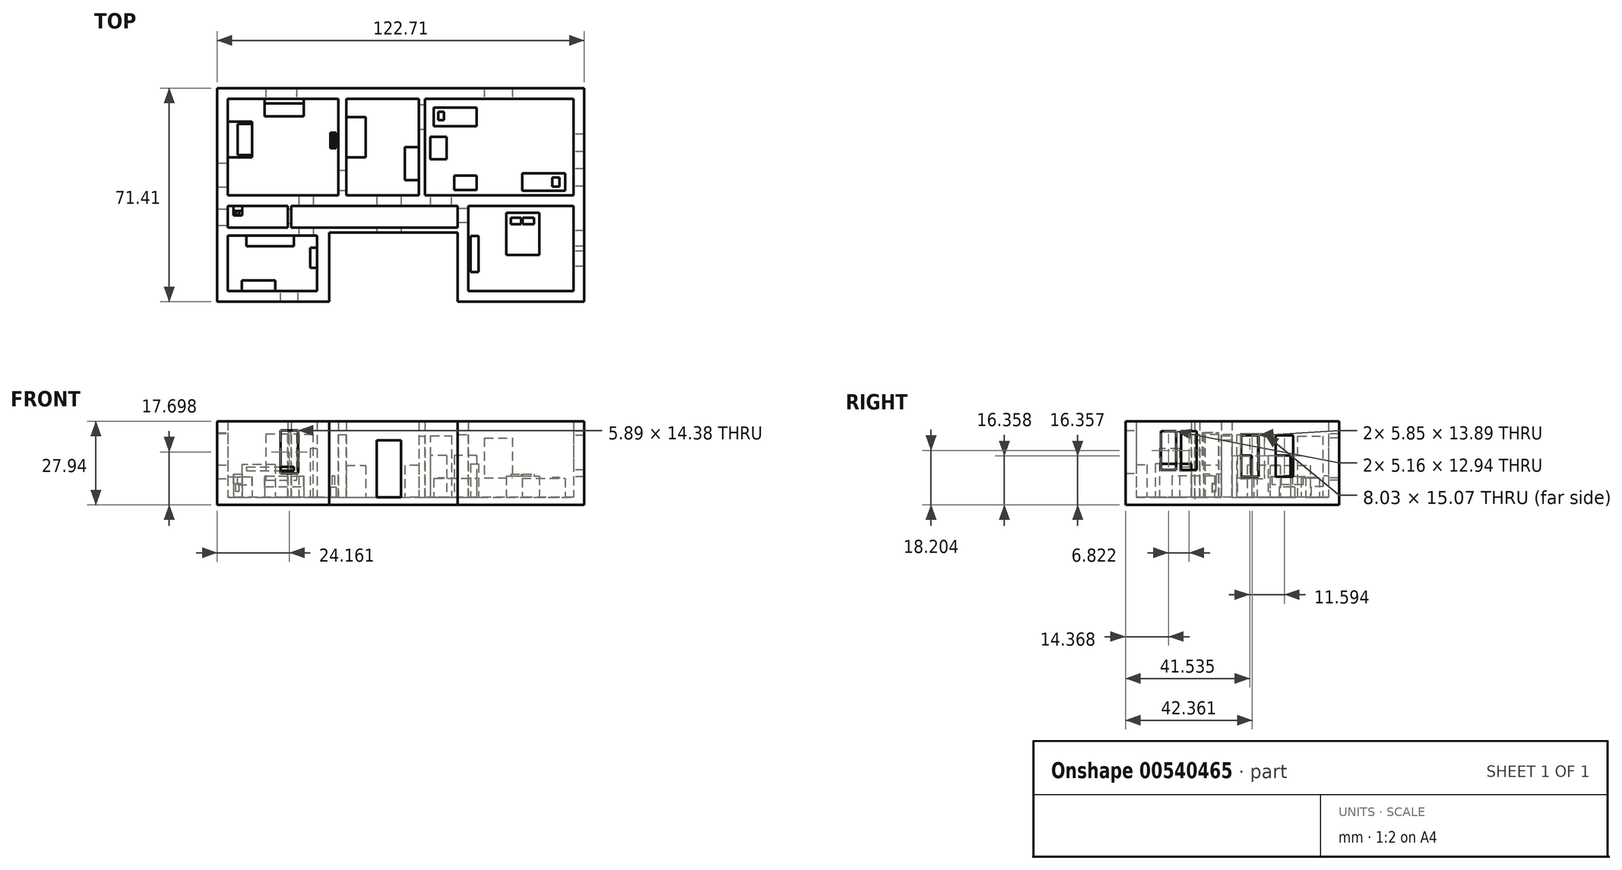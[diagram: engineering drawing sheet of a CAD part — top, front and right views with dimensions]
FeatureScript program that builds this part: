
annotation { "Feature Type Name" : "Feature", "Feature Type Description" : "" }
export const myFeature = defineFeature(function(context is Context, id is Id, definition is map)
    precondition{}
    {
        {
            var Q0;
            Q0=qCreatedBy(makeId("Top.planeOp"),FACE);
            var sketch = newSketch(context, id + "F0", { "sketchPlane" : qUnion([Q0])});
            skLineSegment(sketch, "E0", {"start": v(-23.01, 3.91) * mm, "end": v(21.3, 3.91) * mm});
            skLineSegment(sketch, "E1", {"start": v(62.73, 39.77) * mm, "end": v(62.73, 7.47) * mm});
            skLineSegment(sketch, "E2", {"start": v(62.73, 3.91) * mm, "end": v(27.52, 3.91) * mm});
            skLineSegment(sketch, "E3", {"start": v(62.73, 3.91) * mm, "end": v(62.73, -24.54) * mm});
            skLineSegment(sketch, "E4", {"start": v(62.73, -24.54) * mm, "end": v(27.52, -24.54) * mm});
            skLineSegment(sketch, "E5", {"start": v(27.52, -24.54) * mm, "end": v(27.52, -3.34) * mm});
            skLineSegment(sketch, "E6", {"start": v(27.52, -3.34) * mm, "end": v(-23.01, -3.34) * mm});
            skLineSegment(sketch, "E7", {"start": v(-23.01, -3.34) * mm, "end": v(-23.01, -24.54) * mm});
            skLineSegment(sketch, "E8", {"start": v(-23.01, -24.54) * mm, "end": v(-52.8, -24.54) * mm});
            skLineSegment(sketch, "E9", {"start": v(-52.8, -24.54) * mm, "end": v(-52.8, -6.04) * mm});
            skLineSegment(sketch, "E10", {"start": v(-52.8, -3.34) * mm, "end": v(-30.46, -3.34) * mm});
            skLineSegment(sketch, "E11", {"start": v(-52.8, -3.34) * mm, "end": v(-52.8, 3.91) * mm});
            skLineSegment(sketch, "E12", {"start": v(-52.8, 7.47) * mm, "end": v(-52.8, 39.77) * mm});
            skLineSegment(sketch, "E13", {"start": v(62.73, 39.77) * mm, "end": v(13.01, 39.77) * mm});
            skLineSegment(sketch, "E14", {"start": v(10.98, 39.77) * mm, "end": v(10.98, 35) * mm});
            skLineSegment(sketch, "E15", {"start": v(-52.8, 39.77) * mm, "end": v(-15.94, 39.77) * mm});
            skLineSegment(sketch, "E16", {"start": v(-15.94, 39.77) * mm, "end": v(-15.94, 11.85) * mm});
            skLineSegment(sketch, "E17.trimOffspring", {"start": v(10.98, 30.8) * mm, "end": v(10.98, 7.47) * mm});
            skLineSegment(sketch, "E18", {"start": v(-56.43, 43.32) * mm, "end": v(-56.43, -28.1) * mm});
            skLineSegment(sketch, "E19", {"start": v(-56.43, -28.1) * mm, "end": v(-19, -28.1) * mm});
            skLineSegment(sketch, "E20", {"start": v(-19, -28.1) * mm, "end": v(-19, -4.99) * mm});
            skLineSegment(sketch, "E21", {"start": v(-19, -4.99) * mm, "end": v(23.96, -4.99) * mm});
            skLineSegment(sketch, "E22", {"start": v(23.96, -4.99) * mm, "end": v(23.96, -28.1) * mm});
            skLineSegment(sketch, "E23", {"start": v(23.96, -28.1) * mm, "end": v(66.28, -28.1) * mm});
            skLineSegment(sketch, "E24", {"start": v(66.28, -28.1) * mm, "end": v(66.28, 43.32) * mm});
            skLineSegment(sketch, "E25", {"start": v(66.28, 43.32) * mm, "end": v(-56.43, 43.32) * mm});
            skLineSegment(sketch, "E26", {"start": v(-52.8, -6.04) * mm, "end": v(-30.46, -6.04) * mm});
            skLineSegment(sketch, "E27", {"start": v(-30.46, -6.04) * mm, "end": v(-30.46, -3.34) * mm});
            skLineSegment(sketch, "E28", {"start": v(-52.8, 3.91) * mm, "end": v(-30.46, 3.91) * mm});
            skLineSegment(sketch, "E29", {"start": v(-30.46, 3.91) * mm, "end": v(-30.46, 7.47) * mm});
            skLineSegment(sketch, "E30", {"start": v(-30.46, 7.47) * mm, "end": v(-52.8, 7.47) * mm});
            skLineSegment(sketch, "E31", {"start": v(-15.94, 7.47) * mm, "end": v(-23.01, 7.47) * mm});
            skLineSegment(sketch, "E32", {"start": v(-23.01, 7.47) * mm, "end": v(-23.01, 3.91) * mm});
            skLineSegment(sketch, "E33", {"start": v(-15.94, 7.47) * mm, "end": v(10.98, 7.47) * mm});
            skLineSegment(sketch, "E34", {"start": v(13.01, 7.47) * mm, "end": v(21.3, 7.47) * mm});
            skLineSegment(sketch, "E35", {"start": v(21.3, 7.47) * mm, "end": v(21.3, 3.91) * mm});
            skLineSegment(sketch, "E36", {"start": v(27.52, 7.47) * mm, "end": v(62.73, 7.47) * mm});
            skLineSegment(sketch, "E37", {"start": v(27.52, 3.91) * mm, "end": v(27.52, 7.47) * mm});
            skLineSegment(sketch, "E38", {"start": v(13.01, 7.47) * mm, "end": v(13.01, 30.8) * mm});
            skLineSegment(sketch, "E39", {"start": v(13.01, 30.8) * mm, "end": v(10.98, 30.8) * mm});
            skLineSegment(sketch, "E40", {"start": v(13.01, 35) * mm, "end": v(13.01, 39.77) * mm});
            skLineSegment(sketch, "E41", {"start": v(10.98, 35) * mm, "end": v(13.01, 35) * mm});
            skLineSegment(sketch, "E42", {"start": v(-13.3, 11.85) * mm, "end": v(-13.3, 39.77) * mm});
            skLineSegment(sketch, "E43", {"start": v(-15.94, 11.85) * mm, "end": v(-13.3, 11.85) * mm});
            skLineSegment(sketch, "E44", {"start": v(-13.3, 39.77) * mm, "end": v(10.98, 39.77) * mm});
            skLineSegment(sketch, "E45", {"start": v(21.3, 3.91) * mm, "end": v(27.52, 3.91) * mm});
            skLineSegment(sketch, "E46", {"start": v(27.52, 7.47) * mm, "end": v(21.3, 7.47) * mm});
            skLineSegment(sketch, "E47", {"start": v(27.52, -3.34) * mm, "end": v(27.52, 3.91) * mm});
            skLineSegment(sketch, "E48", {"start": v(-30.46, -3.34) * mm, "end": v(-23.01, -3.34) * mm});
            skLineSegment(sketch, "E49", {"start": v(-30.46, -6.04) * mm, "end": v(-23.01, -6.04) * mm});
            skLineSegment(sketch, "E50", {"start": v(-23.01, 3.91) * mm, "end": v(-30.46, 3.91) * mm});
            skLineSegment(sketch, "E51", {"start": v(-30.46, 7.47) * mm, "end": v(-23.01, 7.47) * mm});
            skLineSegment(sketch, "E52", {"start": v(10.98, 30.8) * mm, "end": v(10.98, 35) * mm});
            skLineSegment(sketch, "E53", {"start": v(13.01, 35) * mm, "end": v(13.01, 30.8) * mm});
            skLineSegment(sketch, "E54", {"start": v(-15.94, 7.47) * mm, "end": v(-15.94, 11.85) * mm});
            skLineSegment(sketch, "E55", {"start": v(-13.3, 11.85) * mm, "end": v(-13.3, 7.47) * mm});
            skLineSegment(sketch, "E56", {"start": v(27.95, 3.91) * mm, "end": v(27.95, -3.34) * mm});
            skLineSegment(sketch, "E57", {"start": v(-30.46, 3.91) * mm, "end": v(-30.46, -3.34) * mm});
            skLineSegment(sketch, "E58", {"start": v(-32.55, 3.91) * mm, "end": v(-32.55, -3.34) * mm});
            skSolve(sketch);
        }
        {
            var Q0;
            Q0 = qSketchRegion(id + "F0", true);
            var Q1;
            Q1=makeQuery(id+"F0.imprint","IMPRINT",FACE,{"disambiguationData":[TD([[makeQuery(id+"F0.imprint","IMPRINT",EDGE,{"derivedFrom":sQuery(id+"F0.wireOp",EDGE,"E29")}),-1.0]])]});
            var Q2;
            Q2=makeQuery(id+"F0.imprint","IMPRINT",FACE,{"disambiguationData":[TD([[makeQuery(id+"F0.imprint","IMPRINT",EDGE,{"derivedFrom":sQuery(id+"F0.wireOp",EDGE,"E43")}),-1.0]])]});
            var Q3;
            Q3=makeQuery(id+"F0.imprint","IMPRINT",FACE,{"disambiguationData":[TD([[makeQuery(id+"F0.imprint","IMPRINT",EDGE,{"derivedFrom":sQuery(id+"F0.wireOp",EDGE,"E0")}),1.0]])]});
            var Q4;
            Q4=makeQuery(id+"F0.imprint","IMPRINT",FACE,{"disambiguationData":[TD([[makeQuery(id+"F0.imprint","IMPRINT",EDGE,{"derivedFrom":sQuery(id+"F0.wireOp",EDGE,"E27")}),-1.0]])]});
            var Q5;
            Q5=makeQuery(id+"F0.imprint","IMPRINT",FACE,{"disambiguationData":[TD([[makeQuery(id+"F0.imprint","IMPRINT",EDGE,{"derivedFrom":sQuery(id+"F0.wireOp",EDGE,"E35")}),1.0]])]});
            var Q6;
            Q6=makeQuery(id+"F0.imprint","IMPRINT",FACE,{"disambiguationData":[TD([[makeQuery(id+"F0.imprint","IMPRINT",EDGE,{"derivedFrom":sQuery(id+"F0.wireOp",EDGE,"E39")}),-1.0]])]});
            var Q7;
            {var subQ0=sQuery(id+"F0.wireOp",EDGE,"E47");Q7=makeQuery(id+"F0.imprint","IMPRINT",FACE,{"disambiguationData":[TD([[makeQuery(id+"F0.imprint","IMPRINT",EDGE,{"derivedFrom":subQ0}),1.0]])]});}
            var Q8;
            {var subQ0=sQuery(id+"F0.wireOp",EDGE,"E57");Q8=makeQuery(id+"F0.imprint","IMPRINT",FACE,{"disambiguationData":[TD([[makeQuery(id+"F0.imprint","IMPRINT",EDGE,{"derivedFrom":subQ0}),-1.0]])]});}
            extrude(context, id + "F1", {"entities" : qUnion([Q0, Q1, Q2, Q3, Q4, Q5, Q6, Q7, Q8]), "depth" : 25.4 * mm, "offsetDistance" : 25.4 * mm});
        }
        {
            var Q0;
            Q0=makeQuery(id+"F1.opExtrude","CAP_FACE",FACE,{"disambiguationData":[OSD([sQuery(id+"F0.wireOp",EDGE,"E0"),sQuery(id+"F0.wireOp",EDGE,"E1"),sQuery(id+"F0.wireOp",EDGE,"E2"),sQuery(id+"F0.wireOp",EDGE,"E3"),sQuery(id+"F0.wireOp",EDGE,"E4"),sQuery(id+"F0.wireOp",EDGE,"E5"),sQuery(id+"F0.wireOp",EDGE,"E6"),sQuery(id+"F0.wireOp",EDGE,"E7"),sQuery(id+"F0.wireOp",EDGE,"E8"),sQuery(id+"F0.wireOp",EDGE,"E9"),sQuery(id+"F0.wireOp",EDGE,"E10"),sQuery(id+"F0.wireOp",EDGE,"E11"),sQuery(id+"F0.wireOp",EDGE,"E12"),sQuery(id+"F0.wireOp",EDGE,"E13"),sQuery(id+"F0.wireOp",EDGE,"E14"),sQuery(id+"F0.wireOp",EDGE,"E15"),sQuery(id+"F0.wireOp",EDGE,"E16"),sQuery(id+"F0.wireOp",EDGE,"E17.trimOffspring"),sQuery(id+"F0.wireOp",EDGE,"E18"),sQuery(id+"F0.wireOp",EDGE,"E19"),sQuery(id+"F0.wireOp",EDGE,"E20"),sQuery(id+"F0.wireOp",EDGE,"E21"),sQuery(id+"F0.wireOp",EDGE,"E22"),sQuery(id+"F0.wireOp",EDGE,"E23"),sQuery(id+"F0.wireOp",EDGE,"E24"),sQuery(id+"F0.wireOp",EDGE,"E25"),sQuery(id+"F0.wireOp",EDGE,"E26"),sQuery(id+"F0.wireOp",EDGE,"E28"),sQuery(id+"F0.wireOp",EDGE,"E30"),sQuery(id+"F0.wireOp",EDGE,"E31"),sQuery(id+"F0.wireOp",EDGE,"E33"),sQuery(id+"F0.wireOp",EDGE,"E34"),sQuery(id+"F0.wireOp",EDGE,"E36"),sQuery(id+"F0.wireOp",EDGE,"E38"),sQuery(id+"F0.wireOp",EDGE,"E40"),sQuery(id+"F0.wireOp",EDGE,"E42"),sQuery(id+"F0.wireOp",EDGE,"E44"),sQuery(id+"F0.wireOp",EDGE,"E45"),sQuery(id+"F0.wireOp",EDGE,"E46"),sQuery(id+"F0.wireOp",EDGE,"E47"),sQuery(id+"F0.wireOp",EDGE,"E48"),sQuery(id+"F0.wireOp",EDGE,"E49"),sQuery(id+"F0.wireOp",EDGE,"E50"),sQuery(id+"F0.wireOp",EDGE,"E51"),sQuery(id+"F0.wireOp",EDGE,"E52"),sQuery(id+"F0.wireOp",EDGE,"E53"),sQuery(id+"F0.wireOp",EDGE,"E54"),sQuery(id+"F0.wireOp",EDGE,"E55"),sQuery(id+"F0.wireOp",EDGE,"E56"),sQuery(id+"F0.wireOp",EDGE,"E57"),sQuery(id+"F0.wireOp",EDGE,"E58")])],"isStart":true});
            var sketch = newSketch(context, id + "F2", { "sketchPlane" : qUnion([Q0])});
            skLineSegment(sketch, "E59.bottom", {"start": v(-56.43, 28.1) * mm, "end": v(66.28, 28.1) * mm});
            skLineSegment(sketch, "E59.top", {"start": v(-56.43, -43.32) * mm, "end": v(66.28, -43.32) * mm});
            skLineSegment(sketch, "E59.left", {"start": v(-56.43, 28.1) * mm, "end": v(-56.43, -43.32) * mm});
            skLineSegment(sketch, "E59.right", {"start": v(66.28, 28.1) * mm, "end": v(66.28, -43.32) * mm});
            skSolve(sketch);
        }
        {
            var Q0;
            Q0 = qSketchRegion(id + "F2", true);
            extrude(context, id + "F3", {"entities" : qUnion([Q0]), "operationType" : NewBodyOperationType.ADD, "depth" : 2.54 * mm, "offsetDistance" : 25.4 * mm});
        }
        {
            var Q0;
            Q0=makeQuery(id+"F1.opExtrude","SWEPT_FACE",FACE,{"disambiguationData":[OSD([sQuery(id+"F0.wireOp",EDGE,"E21")])]});
            var sketch = newSketch(context, id + "F4", { "sketchPlane" : qUnion([Q0])});
            skLineSegment(sketch, "E60", {"start": v(-3.06, 0) * mm, "end": v(-3.06, 19.08) * mm});
            skLineSegment(sketch, "E61", {"start": v(-3.06, 19.08) * mm, "end": v(5.05, 19.08) * mm});
            skLineSegment(sketch, "E62", {"start": v(5.05, 19.08) * mm, "end": v(5.05, 0) * mm});
            skSolve(sketch);
        }
        {
            var Q0;
            Q0=makeQuery(id+"F1.opExtrude","SWEPT_FACE",FACE,{"disambiguationData":[OSD([sQuery(id+"F0.wireOp",EDGE,"E5"),sQuery(id+"F0.wireOp",EDGE,"E47")])]});
            var sketch = newSketch(context, id + "F5", { "sketchPlane" : qUnion([Q0])});
            skLineSegment(sketch, "E63", {"start": v(-1.5, 0) * mm, "end": v(-1.5, 21) * mm});
            skLineSegment(sketch, "E64", {"start": v(-1.5, 21) * mm, "end": v(3.2, 21) * mm});
            skLineSegment(sketch, "E65", {"start": v(3.2, 21) * mm, "end": v(3.2, 0) * mm});
            skSolve(sketch);
        }
        {
            var Q0;
            Q0=makeQuery(id+"F1.opExtrude","SWEPT_FACE",FACE,{"disambiguationData":[OSD([sQuery(id+"F0.wireOp",EDGE,"E26"),sQuery(id+"F0.wireOp",EDGE,"E49")])]});
            var sketch = newSketch(context, id + "F6", { "sketchPlane" : qUnion([Q0])});
            skLineSegment(sketch, "E66", {"start": v(-29.15, 0) * mm, "end": v(-29.15, 20.99) * mm});
            skLineSegment(sketch, "E67", {"start": v(-29.15, 20.99) * mm, "end": v(-24.32, 20.99) * mm});
            skLineSegment(sketch, "E68", {"start": v(-24.32, 20.99) * mm, "end": v(-24.32, 0) * mm});
            skSolve(sketch);
        }
        {
            var Q0;
            Q0=makeQuery(id+"F1.opExtrude","SWEPT_FACE",FACE,{"disambiguationData":[OSD([sQuery(id+"F0.wireOp",EDGE,"E42"),sQuery(id+"F0.wireOp",EDGE,"E55")])]});
            var sketch = newSketch(context, id + "F7", { "sketchPlane" : qUnion([Q0])});
            skLineSegment(sketch, "E69", {"start": v(9.12, 0) * mm, "end": v(9.12, 20.96) * mm});
            skLineSegment(sketch, "E70", {"start": v(9.12, 20.96) * mm, "end": v(15.83, 20.96) * mm});
            skLineSegment(sketch, "E71", {"start": v(15.83, 20.96) * mm, "end": v(15.83, 0) * mm});
            skSolve(sketch);
        }
        {
            var Q0;
            Q0=makeQuery(id+"F1.opExtrude","SWEPT_FACE",FACE,{"disambiguationData":[OSD([sQuery(id+"F0.wireOp",EDGE,"E38"),sQuery(id+"F0.wireOp",EDGE,"E40"),sQuery(id+"F0.wireOp",EDGE,"E53")])]});
            var sketch = newSketch(context, id + "F8", { "sketchPlane" : qUnion([Q0])});
            skLineSegment(sketch, "E72", {"start": v(29.52, 0) * mm, "end": v(29.52, 20.52) * mm});
            skLineSegment(sketch, "E73", {"start": v(29.52, 20.52) * mm, "end": v(37.83, 20.52) * mm});
            skLineSegment(sketch, "E74", {"start": v(37.83, 20.52) * mm, "end": v(37.83, 0) * mm});
            skSolve(sketch);
        }
        {
            var Q0;
            Q0=makeQuery(id+"F1.opExtrude","SWEPT_FACE",FACE,{"disambiguationData":[OSD([sQuery(id+"F0.wireOp",EDGE,"E34"),sQuery(id+"F0.wireOp",EDGE,"E36"),sQuery(id+"F0.wireOp",EDGE,"E46")])]});
            var sketch = newSketch(context, id + "F9", { "sketchPlane" : qUnion([Q0])});
            skLineSegment(sketch, "E75", {"start": v(-14.91, 0) * mm, "end": v(-14.91, 20.6) * mm});
            skLineSegment(sketch, "E76", {"start": v(-14.91, 20.6) * mm, "end": v(-21.93, 20.6) * mm});
            skLineSegment(sketch, "E77", {"start": v(-21.93, 20.6) * mm, "end": v(-21.93, 0) * mm});
            skSolve(sketch);
        }
        {
            var Q0;
            {var subQ0=sQuery(id+"F0.wireOp",EDGE,"E46");var subQ1=sQuery(id+"F0.wireOp",EDGE,"E36");var subQ2=sQuery(id+"F0.wireOp",EDGE,"E34");var subQ3=sQuery(id+"F0.wireOp",EDGE,"E53");var subQ4=sQuery(id+"F0.wireOp",EDGE,"E40");var subQ5=sQuery(id+"F0.wireOp",EDGE,"E38");var subQ6=sQuery(id+"F0.wireOp",EDGE,"E55");var subQ7=sQuery(id+"F0.wireOp",EDGE,"E42");var subQ8=sQuery(id+"F0.wireOp",EDGE,"E57");var subQ9=sQuery(id+"F0.wireOp",EDGE,"E49");var subQ10=sQuery(id+"F0.wireOp",EDGE,"E26");var subQ11=sQuery(id+"F0.wireOp",EDGE,"E47");var subQ12=sQuery(id+"F0.wireOp",EDGE,"E5");var subQ13=sQuery(id+"F0.wireOp",EDGE,"E21");var subQ14=sQuery(id+"F2.wireOp",EDGE,"E59.bottom");var subQ15=makeQuery(id+"F3.opExtrude","CAP_FACE",FACE,{"disambiguationData":[OSD([subQ14,sQuery(id+"F2.wireOp",EDGE,"E59.top"),sQuery(id+"F2.wireOp",EDGE,"E59.left"),sQuery(id+"F2.wireOp",EDGE,"E59.right")])],"isStart":true});Q0=makeQuery(id+"F1OyW4JsobVm1jb_1.boolean.opBoolean","MERGE",FACE,{"derivedFrom":[makeQuery(id+"FLEFhuE11UkbnLt_1.boolean.opBoolean","MERGE",FACE,{"derivedFrom":[makeQuery(id+"F3.boolean.opBoolean","SPLIT",FACE,{"disambiguationData":[TD([makeQuery(id+"F1.opExtrude","SWEPT_FACE",FACE,{"disambiguationData":[OSD([sQuery(id+"F0.wireOp",EDGE,"E1")])]})])],"derivedFrom":subQ15}),makeQuery(id+"FrTdRAxnjzJTjCx_1.boolean.opBoolean","MERGE",FACE,{"derivedFrom":[makeQuery(id+"F3DeUZIcQ9rfyYD_1.boolean.opBoolean","MERGE",FACE,{"derivedFrom":[makeQuery(id+"F3.boolean.opBoolean","SPLIT",FACE,{"disambiguationData":[TD([makeQuery(id+"F1.opExtrude","SWEPT_FACE",FACE,{"disambiguationData":[OSD([sQuery(id+"F0.wireOp",EDGE,"E10")])]})])],"derivedFrom":subQ15}),makeQuery(id+"FgtxtSheF1BaROL_1.boolean.opBoolean","MERGE",FACE,{"derivedFrom":[makeQuery(id+"F3.boolean.opBoolean","SPLIT",FACE,{"disambiguationData":[TD([makeQuery(id+"F1.opExtrude","SWEPT_FACE",FACE,{"disambiguationData":[OSD([sQuery(id+"F0.wireOp",EDGE,"E7")])]})])],"derivedFrom":subQ15}),makeQuery(id+"F3.boolean.opBoolean","SPLIT",FACE,{"disambiguationData":[TD([makeQuery(id+"F1.opExtrude","SWEPT_FACE",FACE,{"disambiguationData":[OSD([sQuery(id+"F0.wireOp",EDGE,"E12")])]})])],"derivedFrom":subQ15}),makeQuery(id+"F2jdueuljUY2eIT_1.boolean.opBoolean","MERGE",FACE,{"derivedFrom":[makeQuery(id+"F3.boolean.opBoolean","SPLIT",FACE,{"disambiguationData":[TD([makeQuery(id+"F1.opExtrude","SWEPT_FACE",FACE,{"disambiguationData":[OSD([sQuery(id+"F0.wireOp",EDGE,"E2")])]})])],"derivedFrom":subQ15}),makeQuery(id+"Fv9FIk8MfVWjiKt_1.boolean.opBoolean","MERGE",FACE,{"derivedFrom":[makeQuery(id+"F3.boolean.opBoolean","SPLIT",FACE,{"disambiguationData":[TD([makeQuery(id+"F1.opExtrude","SWEPT_FACE",FACE,{"disambiguationData":[OSD([sQuery(id+"F0.wireOp",EDGE,"E56")])]})])],"derivedFrom":subQ15}),makeQuery(id+"F3.boolean.opBoolean","SPLIT",FACE,{"disambiguationData":[TD([makeQuery(id+"F1.opExtrude","SWEPT_FACE",FACE,{"disambiguationData":[OSD([sQuery(id+"F0.wireOp",EDGE,"E33")])]})])],"derivedFrom":subQ15}),makeQuery(id+"F3.boolean.opBoolean","SPLIT",FACE,{"disambiguationData":[TD([makeQuery(id+"F1.opExtrude","SWEPT_FACE",FACE,{"disambiguationData":[OSD([sQuery(id+"F0.wireOp",EDGE,"E19")])]})])],"derivedFrom":subQ15}),makeQuery(id+"Fv9FIk8MfVWjiKt_1.opExtrude","SWEPT_FACE",FACE,{"disambiguationData":[OSD([subQ13])]})]}),makeQuery(id+"F2jdueuljUY2eIT_1.opExtrude","SWEPT_FACE",FACE,{"disambiguationData":[OSD([subQ12,subQ11])]})]}),makeQuery(id+"FgtxtSheF1BaROL_1.opExtrude","SWEPT_FACE",FACE,{"disambiguationData":[OSD([subQ10,subQ9])]})]}),makeQuery(id+"F3DeUZIcQ9rfyYD_1.opExtrude","SWEPT_FACE",FACE,{"disambiguationData":[OSD([subQ8])]})]}),makeQuery(id+"FrTdRAxnjzJTjCx_1.opExtrude","SWEPT_FACE",FACE,{"disambiguationData":[OSD([subQ7,subQ6])]})]}),makeQuery(id+"FLEFhuE11UkbnLt_1.opExtrude","SWEPT_FACE",FACE,{"disambiguationData":[OSD([subQ5,subQ4,subQ3])]})]}),makeQuery(id+"F1OyW4JsobVm1jb_1.opExtrude","SWEPT_FACE",FACE,{"disambiguationData":[OSD([subQ2,subQ1,subQ0])]})]});}
            var sketch = newSketch(context, id + "F10", { "sketchPlane" : qUnion([Q0])});
            skLineSegment(sketch, "E78.bottom", {"start": v(-19, -4.99) * mm, "end": v(23.96, -4.99) * mm});
            skLineSegment(sketch, "E78.top", {"start": v(-19, -28.1) * mm, "end": v(23.96, -28.1) * mm});
            skLineSegment(sketch, "E78.left", {"start": v(-19, -4.99) * mm, "end": v(-19, -28.1) * mm});
            skLineSegment(sketch, "E78.right", {"start": v(23.96, -4.99) * mm, "end": v(23.96, -28.1) * mm});
            skSolve(sketch);
        }
        {
            var Q0;
            Q0 = qSketchRegion(id + "F10", true);
            extrude(context, id + "F11", {"entities" : qUnion([Q0]), "operationType" : NewBodyOperationType.REMOVE, "oppositeDirection" : true, "depth" : 25.4 * mm, "offsetDistance" : 25.4 * mm});
        }
        {
            var Q0;
            Q0=makeQuery(id+"F1.opExtrude","CAP_FACE",FACE,{"disambiguationData":[OSD([sQuery(id+"F0.wireOp",EDGE,"E1"),sQuery(id+"F0.wireOp",EDGE,"E2"),sQuery(id+"F0.wireOp",EDGE,"E3"),sQuery(id+"F0.wireOp",EDGE,"E4"),sQuery(id+"F0.wireOp",EDGE,"E5"),sQuery(id+"F0.wireOp",EDGE,"E7"),sQuery(id+"F0.wireOp",EDGE,"E8"),sQuery(id+"F0.wireOp",EDGE,"E9"),sQuery(id+"F0.wireOp",EDGE,"E10"),sQuery(id+"F0.wireOp",EDGE,"E11"),sQuery(id+"F0.wireOp",EDGE,"E12"),sQuery(id+"F0.wireOp",EDGE,"E13"),sQuery(id+"F0.wireOp",EDGE,"E14"),sQuery(id+"F0.wireOp",EDGE,"E15"),sQuery(id+"F0.wireOp",EDGE,"E16"),sQuery(id+"F0.wireOp",EDGE,"E17.trimOffspring"),sQuery(id+"F0.wireOp",EDGE,"E18"),sQuery(id+"F0.wireOp",EDGE,"E19"),sQuery(id+"F0.wireOp",EDGE,"E20"),sQuery(id+"F0.wireOp",EDGE,"E21"),sQuery(id+"F0.wireOp",EDGE,"E22"),sQuery(id+"F0.wireOp",EDGE,"E23"),sQuery(id+"F0.wireOp",EDGE,"E24"),sQuery(id+"F0.wireOp",EDGE,"E25"),sQuery(id+"F0.wireOp",EDGE,"E26"),sQuery(id+"F0.wireOp",EDGE,"E28"),sQuery(id+"F0.wireOp",EDGE,"E30"),sQuery(id+"F0.wireOp",EDGE,"E31"),sQuery(id+"F0.wireOp",EDGE,"E33"),sQuery(id+"F0.wireOp",EDGE,"E34"),sQuery(id+"F0.wireOp",EDGE,"E36"),sQuery(id+"F0.wireOp",EDGE,"E38"),sQuery(id+"F0.wireOp",EDGE,"E40"),sQuery(id+"F0.wireOp",EDGE,"E42"),sQuery(id+"F0.wireOp",EDGE,"E44"),sQuery(id+"F0.wireOp",EDGE,"E46"),sQuery(id+"F0.wireOp",EDGE,"E47"),sQuery(id+"F0.wireOp",EDGE,"E49"),sQuery(id+"F0.wireOp",EDGE,"E51"),sQuery(id+"F0.wireOp",EDGE,"E52"),sQuery(id+"F0.wireOp",EDGE,"E53"),sQuery(id+"F0.wireOp",EDGE,"E54"),sQuery(id+"F0.wireOp",EDGE,"E55"),sQuery(id+"F0.wireOp",EDGE,"E58")])],"isStart":false});
            var sketch = newSketch(context, id + "F12", { "sketchPlane" : qUnion([Q0])});
            skLineSegment(sketch, "E79.bottom", {"start": v(-28.74, 3.91) * mm, "end": v(23.96, 3.91) * mm});
            skLineSegment(sketch, "E79.top", {"start": v(-28.74, -3.34) * mm, "end": v(23.96, -3.34) * mm});
            skLineSegment(sketch, "E79.left", {"start": v(-28.74, 3.91) * mm, "end": v(-28.74, -3.34) * mm});
            skLineSegment(sketch, "E79.right", {"start": v(23.96, 3.91) * mm, "end": v(23.96, -3.34) * mm});
            skSolve(sketch);
        }
        {
            var Q0;
            Q0=makeQuery(id+"F12.imprint","IMPRINT",FACE,{"disambiguationData":[TD([[makeQuery(id+"F12.imprint","IMPRINT",EDGE,{"derivedFrom":sQuery(id+"F12.wireOp",EDGE,"E79.bottom")}),-1.0]])]});
            var Q1;
            Q1=makeQuery(id+"F3.opExtrude","CAP_FACE",FACE,{"disambiguationData":[OSD([sQuery(id+"F2.wireOp",EDGE,"E59.bottom"),sQuery(id+"F2.wireOp",EDGE,"E59.top"),sQuery(id+"F2.wireOp",EDGE,"E59.left"),sQuery(id+"F2.wireOp",EDGE,"E59.right")])],"isStart":false});
            extrude(context, id + "F13", {"entities" : qUnion([Q0]), "operationType" : NewBodyOperationType.REMOVE, "oppositeDirection" : true, "depth" : 25.4 * mm, "endBoundEntityFace" : qUnion([Q1]), "offsetDistance" : 25.4 * mm});
        }
        {
            var Q0;
            Q0=makeQuery(id+"F1.opExtrude","CAP_FACE",FACE,{"disambiguationData":[OSD([sQuery(id+"F0.wireOp",EDGE,"E1"),sQuery(id+"F0.wireOp",EDGE,"E2"),sQuery(id+"F0.wireOp",EDGE,"E3"),sQuery(id+"F0.wireOp",EDGE,"E4"),sQuery(id+"F0.wireOp",EDGE,"E5"),sQuery(id+"F0.wireOp",EDGE,"E7"),sQuery(id+"F0.wireOp",EDGE,"E8"),sQuery(id+"F0.wireOp",EDGE,"E9"),sQuery(id+"F0.wireOp",EDGE,"E10"),sQuery(id+"F0.wireOp",EDGE,"E11"),sQuery(id+"F0.wireOp",EDGE,"E12"),sQuery(id+"F0.wireOp",EDGE,"E13"),sQuery(id+"F0.wireOp",EDGE,"E14"),sQuery(id+"F0.wireOp",EDGE,"E15"),sQuery(id+"F0.wireOp",EDGE,"E16"),sQuery(id+"F0.wireOp",EDGE,"E17.trimOffspring"),sQuery(id+"F0.wireOp",EDGE,"E18"),sQuery(id+"F0.wireOp",EDGE,"E19"),sQuery(id+"F0.wireOp",EDGE,"E20"),sQuery(id+"F0.wireOp",EDGE,"E21"),sQuery(id+"F0.wireOp",EDGE,"E22"),sQuery(id+"F0.wireOp",EDGE,"E23"),sQuery(id+"F0.wireOp",EDGE,"E24"),sQuery(id+"F0.wireOp",EDGE,"E25"),sQuery(id+"F0.wireOp",EDGE,"E26"),sQuery(id+"F0.wireOp",EDGE,"E28"),sQuery(id+"F0.wireOp",EDGE,"E30"),sQuery(id+"F0.wireOp",EDGE,"E31"),sQuery(id+"F0.wireOp",EDGE,"E33"),sQuery(id+"F0.wireOp",EDGE,"E34"),sQuery(id+"F0.wireOp",EDGE,"E36"),sQuery(id+"F0.wireOp",EDGE,"E38"),sQuery(id+"F0.wireOp",EDGE,"E40"),sQuery(id+"F0.wireOp",EDGE,"E42"),sQuery(id+"F0.wireOp",EDGE,"E44"),sQuery(id+"F0.wireOp",EDGE,"E46"),sQuery(id+"F0.wireOp",EDGE,"E47"),sQuery(id+"F0.wireOp",EDGE,"E49"),sQuery(id+"F0.wireOp",EDGE,"E51"),sQuery(id+"F0.wireOp",EDGE,"E52"),sQuery(id+"F0.wireOp",EDGE,"E53"),sQuery(id+"F0.wireOp",EDGE,"E54"),sQuery(id+"F0.wireOp",EDGE,"E55"),sQuery(id+"F0.wireOp",EDGE,"E58")])],"isStart":false});
            var sketch = newSketch(context, id + "F14", { "sketchPlane" : qUnion([Q0])});
            skLineSegment(sketch, "E80.bottom", {"start": v(-32.55, -3.34) * mm, "end": v(-28.74, -3.34) * mm});
            skLineSegment(sketch, "E80.top", {"start": v(-32.55, 3.91) * mm, "end": v(-28.74, 3.91) * mm});
            skLineSegment(sketch, "E80.left", {"start": v(-32.55, -3.34) * mm, "end": v(-32.55, 3.91) * mm});
            skLineSegment(sketch, "E80.right", {"start": v(-28.74, -3.34) * mm, "end": v(-28.74, 3.91) * mm});
            skSolve(sketch);
        }
        {
            var Q0;
            Q0=makeQuery(id+"F14.imprint","IMPRINT",FACE,{"disambiguationData":[TD([[makeQuery(id+"F14.imprint","IMPRINT",EDGE,{"derivedFrom":sQuery(id+"F14.wireOp",EDGE,"E80.bottom")}),1.0]])]});
            extrude(context, id + "F15", {"entities" : qUnion([Q0]), "operationType" : NewBodyOperationType.REMOVE, "oppositeDirection" : true, "depth" : 25.4 * mm, "offsetDistance" : 25.4 * mm});
        }
        {
            var Q0;
            {var subQ0=sQuery(id+"F0.wireOp",EDGE,"E49");var subQ1=sQuery(id+"F0.wireOp",EDGE,"E26");var subQ2=sQuery(id+"F0.wireOp",EDGE,"E46");var subQ3=sQuery(id+"F0.wireOp",EDGE,"E36");var subQ4=sQuery(id+"F0.wireOp",EDGE,"E34");var subQ5=sQuery(id+"F0.wireOp",EDGE,"E53");var subQ6=sQuery(id+"F0.wireOp",EDGE,"E40");var subQ7=sQuery(id+"F0.wireOp",EDGE,"E38");var subQ8=sQuery(id+"F0.wireOp",EDGE,"E55");var subQ9=sQuery(id+"F0.wireOp",EDGE,"E42");var subQ10=sQuery(id+"F2.wireOp",EDGE,"E59.bottom");var subQ11=makeQuery(id+"F3.opExtrude","CAP_FACE",FACE,{"disambiguationData":[OSD([subQ10,sQuery(id+"F2.wireOp",EDGE,"E59.top"),sQuery(id+"F2.wireOp",EDGE,"E59.left"),sQuery(id+"F2.wireOp",EDGE,"E59.right")])],"isStart":true});var subQ12=sQuery(id+"F0.wireOp",EDGE,"E47");var subQ13=sQuery(id+"F0.wireOp",EDGE,"E5");var subQ14=sQuery(id+"F0.wireOp",EDGE,"E21");Q0=makeQuery(id+"F15.boolean.opBoolean","MERGE",FACE,{"derivedFrom":[makeQuery(id+"Fj91QTaVXWuzYNv_1.boolean.opBoolean","MERGE",FACE,{"derivedFrom":[makeQuery(id+"F3.boolean.opBoolean","SPLIT",FACE,{"disambiguationData":[TD([makeQuery(id+"F1.opExtrude","SWEPT_FACE",FACE,{"disambiguationData":[OSD([sQuery(id+"F0.wireOp",EDGE,"E10")])]})])],"derivedFrom":subQ11}),makeQuery(id+"F13.boolean.opBoolean","MERGE",FACE,{"derivedFrom":[makeQuery(id+"F1OyW4JsobVm1jb_1.boolean.opBoolean","MERGE",FACE,{"derivedFrom":[makeQuery(id+"FLEFhuE11UkbnLt_1.boolean.opBoolean","MERGE",FACE,{"derivedFrom":[makeQuery(id+"F3.boolean.opBoolean","SPLIT",FACE,{"disambiguationData":[TD([makeQuery(id+"F1.opExtrude","SWEPT_FACE",FACE,{"disambiguationData":[OSD([sQuery(id+"F0.wireOp",EDGE,"E1")])]})])],"derivedFrom":subQ11}),makeQuery(id+"FrTdRAxnjzJTjCx_1.boolean.opBoolean","MERGE",FACE,{"derivedFrom":[makeQuery(id+"F2jdueuljUY2eIT_1.boolean.opBoolean","MERGE",FACE,{"derivedFrom":[makeQuery(id+"F3.boolean.opBoolean","SPLIT",FACE,{"disambiguationData":[TD([makeQuery(id+"F1.opExtrude","SWEPT_FACE",FACE,{"disambiguationData":[OSD([sQuery(id+"F0.wireOp",EDGE,"E2")])]})])],"derivedFrom":subQ11}),makeQuery(id+"Fv9FIk8MfVWjiKt_1.boolean.opBoolean","MERGE",FACE,{"derivedFrom":[makeQuery(id+"F3.boolean.opBoolean","SPLIT",FACE,{"disambiguationData":[TD([makeQuery(id+"F1.opExtrude","SWEPT_FACE",FACE,{"disambiguationData":[OSD([sQuery(id+"F0.wireOp",EDGE,"E33")])]})])],"derivedFrom":subQ11}),makeQuery(id+"F3.boolean.opBoolean","SPLIT",FACE,{"disambiguationData":[TD([makeQuery(id+"F1.opExtrude","SWEPT_FACE",FACE,{"disambiguationData":[OSD([sQuery(id+"F0.wireOp",EDGE,"E19")])]})])],"derivedFrom":subQ11}),makeQuery(id+"Fv9FIk8MfVWjiKt_1.opExtrude","SWEPT_FACE",FACE,{"disambiguationData":[OSD([subQ14])]})]}),makeQuery(id+"F2jdueuljUY2eIT_1.opExtrude","SWEPT_FACE",FACE,{"disambiguationData":[OSD([subQ13,subQ12])]})]}),makeQuery(id+"FgtxtSheF1BaROL_1.boolean.opBoolean","MERGE",FACE,{"derivedFrom":[makeQuery(id+"F3.boolean.opBoolean","SPLIT",FACE,{"disambiguationData":[TD([makeQuery(id+"F1.opExtrude","SWEPT_FACE",FACE,{"disambiguationData":[OSD([sQuery(id+"F0.wireOp",EDGE,"E7")])]})])],"derivedFrom":subQ11}),makeQuery(id+"F3.boolean.opBoolean","SPLIT",FACE,{"disambiguationData":[TD([makeQuery(id+"F1.opExtrude","SWEPT_FACE",FACE,{"disambiguationData":[OSD([sQuery(id+"F0.wireOp",EDGE,"E12")])]})])],"derivedFrom":subQ11}),makeQuery(id+"FgtxtSheF1BaROL_1.opExtrude","SWEPT_FACE",FACE,{"disambiguationData":[OSD([subQ1,subQ0])]})]}),makeQuery(id+"FrTdRAxnjzJTjCx_1.opExtrude","SWEPT_FACE",FACE,{"disambiguationData":[OSD([subQ9,subQ8])]})]}),makeQuery(id+"FLEFhuE11UkbnLt_1.opExtrude","SWEPT_FACE",FACE,{"disambiguationData":[OSD([subQ7,subQ6,subQ5])]})]}),makeQuery(id+"F1OyW4JsobVm1jb_1.opExtrude","SWEPT_FACE",FACE,{"disambiguationData":[OSD([subQ4,subQ3,subQ2])]})]}),makeQuery(id+"F13.opExtrude","CAP_FACE",FACE,{"disambiguationData":[OSD([sQuery(id+"F12.wireOp",EDGE,"E79.bottom"),sQuery(id+"F12.wireOp",EDGE,"E79.top"),sQuery(id+"F12.wireOp",EDGE,"E79.left"),sQuery(id+"F12.wireOp",EDGE,"E79.right")])],"isStart":false})]}),makeQuery(id+"Fj91QTaVXWuzYNv_1.opExtrude","SWEPT_FACE",FACE,{"disambiguationData":[OSD([subQ1,subQ0,sQuery(id+"F6.wireOp",EDGE,"RrXdWSjr-arhV-RAkg-Kmuo-RMM0U9ZidCex")])]})]}),makeQuery(id+"F15.opExtrude","CAP_FACE",FACE,{"disambiguationData":[OSD([sQuery(id+"F14.wireOp",EDGE,"E80.bottom"),sQuery(id+"F14.wireOp",EDGE,"E80.top"),sQuery(id+"F14.wireOp",EDGE,"E80.left"),sQuery(id+"F14.wireOp",EDGE,"E80.right")])],"isStart":false})]});}
            var sketch = newSketch(context, id + "F16", { "sketchPlane" : qUnion([Q0])});
            skLineSegment(sketch, "E81", {"start": v(-32.8, 3.91) * mm, "end": v(-32.8, -3.34) * mm});
            skLineSegment(sketch, "E82", {"start": v(-31.65, 3.91) * mm, "end": v(-31.65, -3.34) * mm});
            skSolve(sketch);
        }
        {
            var Q0;
            {var subQ0=sQuery(id+"F16.wireOp",EDGE,"E81");Q0=makeQuery(id+"F16.imprint","IMPRINT",FACE,{"disambiguationData":[TD([[makeQuery(id+"F16.imprint","IMPRINT",EDGE,{"derivedFrom":subQ0}),1.0]])]});}
            extrude(context, id + "F17", {"entities" : qUnion([Q0]), "operationType" : NewBodyOperationType.ADD, "depth" : 25.4 * mm, "offsetDistance" : 25.4 * mm});
        }
        {
            var Q0;
            Q0=makeQuery(id+"F17.opExtrude","SWEPT_FACE",FACE,{"disambiguationData":[OSD([sQuery(id+"F16.wireOp",EDGE,"E82")])]});
            var sketch = newSketch(context, id + "F18", { "sketchPlane" : qUnion([Q0])});
            skLineSegment(sketch, "E83", {"start": v(-1.9, 0) * mm, "end": v(-1.9, 21.75) * mm});
            skLineSegment(sketch, "E84", {"start": v(-1.9, 21.75) * mm, "end": v(2.93, 21.75) * mm});
            skLineSegment(sketch, "E85", {"start": v(2.93, 21.75) * mm, "end": v(2.93, 0) * mm});
            skSolve(sketch);
        }
        {
            var Q0;
            {var subQ0=sQuery(id+"F18.wireOp",EDGE,"E83");Q0=makeQuery(id+"F18.imprint","IMPRINT",FACE,{"disambiguationData":[TD([[makeQuery(id+"F18.imprint","IMPRINT",EDGE,{"derivedFrom":subQ0}),-1.0]])]});}
            extrude(context, id + "F19", {"entities" : qUnion([Q0]), "operationType" : NewBodyOperationType.REMOVE, "oppositeDirection" : true, "depth" : 6.35 * mm, "offsetDistance" : 25.4 * mm});
        }
        {
            var Q0;
            {var subQ0=sQuery(id+"F8.wireOp",EDGE,"E72");Q0=makeQuery(id+"F8.imprint","IMPRINT",FACE,{"disambiguationData":[TD([[makeQuery(id+"F8.imprint","IMPRINT",EDGE,{"derivedFrom":subQ0}),-1.0]])]});}
            extrude(context, id + "F20", {"entities" : qUnion([Q0]), "operationType" : NewBodyOperationType.REMOVE, "oppositeDirection" : true, "depth" : 6.35 * mm, "offsetDistance" : 25.4 * mm});
        }
        {
            var Q0;
            {var subQ0=sQuery(id+"F4.wireOp",EDGE,"E60");Q0=makeQuery(id+"F4.imprint","IMPRINT",FACE,{"disambiguationData":[TD([[makeQuery(id+"F4.imprint","IMPRINT",EDGE,{"derivedFrom":subQ0}),-1.0]])]});}
            extrude(context, id + "F21", {"entities" : qUnion([Q0]), "operationType" : NewBodyOperationType.REMOVE, "oppositeDirection" : true, "depth" : 25.4 * mm, "offsetDistance" : 25.4 * mm});
        }
        {
            var Q0;
            {var subQ0=sQuery(id+"F9.wireOp",EDGE,"E75");Q0=makeQuery(id+"F9.imprint","IMPRINT",FACE,{"disambiguationData":[TD([[makeQuery(id+"F9.imprint","IMPRINT",EDGE,{"derivedFrom":subQ0}),1.0]])]});}
            extrude(context, id + "F22", {"entities" : qUnion([Q0]), "operationType" : NewBodyOperationType.REMOVE, "oppositeDirection" : true, "depth" : 6.35 * mm, "offsetDistance" : 25.4 * mm});
        }
        {
            var Q0;
            {var subQ0=sQuery(id+"F5.wireOp",EDGE,"E63");Q0=makeQuery(id+"F5.imprint","IMPRINT",FACE,{"disambiguationData":[TD([[makeQuery(id+"F5.imprint","IMPRINT",EDGE,{"derivedFrom":subQ0}),-1.0]])]});}
            extrude(context, id + "F23", {"entities" : qUnion([Q0]), "operationType" : NewBodyOperationType.REMOVE, "oppositeDirection" : true, "depth" : 25.4 * mm, "offsetDistance" : 25.4 * mm});
        }
        {
            var Q0;
            {var subQ0=sQuery(id+"F6.wireOp",EDGE,"E66");Q0=makeQuery(id+"F6.imprint","IMPRINT",FACE,{"disambiguationData":[TD([[makeQuery(id+"F6.imprint","IMPRINT",EDGE,{"derivedFrom":subQ0}),-1.0]])]});}
            extrude(context, id + "F24", {"entities" : qUnion([Q0]), "operationType" : NewBodyOperationType.REMOVE, "oppositeDirection" : true, "depth" : 25.4 * mm, "offsetDistance" : 25.4 * mm});
        }
        {
            var Q0;
            {var subQ0=sQuery(id+"F7.wireOp",EDGE,"E69");Q0=makeQuery(id+"F7.imprint","IMPRINT",FACE,{"disambiguationData":[TD([[makeQuery(id+"F7.imprint","IMPRINT",EDGE,{"derivedFrom":subQ0}),-1.0]])]});}
            extrude(context, id + "F25", {"entities" : qUnion([Q0]), "operationType" : NewBodyOperationType.REMOVE, "oppositeDirection" : true, "depth" : 25.4 * mm, "offsetDistance" : 25.4 * mm});
        }
        {
            var Q0;
            Q0=makeQuery(id+"F1.opExtrude","SWEPT_FACE",FACE,{"disambiguationData":[OSD([sQuery(id+"F0.wireOp",EDGE,"E1")])]});
            var sketch = newSketch(context, id + "F26", { "sketchPlane" : qUnion([Q0])});
            skLineSegment(sketch, "E86.bottom", {"start": v(-27.96, 20.77) * mm, "end": v(-22.11, 20.77) * mm});
            skLineSegment(sketch, "E86.top", {"start": v(-27.96, 6.87) * mm, "end": v(-22.11, 6.87) * mm});
            skLineSegment(sketch, "E86.left", {"start": v(-27.96, 20.77) * mm, "end": v(-27.96, 6.87) * mm});
            skLineSegment(sketch, "E86.right", {"start": v(-22.11, 20.77) * mm, "end": v(-22.11, 6.87) * mm});
            skLineSegment(sketch, "E87.MirrorCS", {"start": v(-16.37, 20.77) * mm, "end": v(-16.37, 6.87) * mm});
            skLineSegment(sketch, "E88.MirrorCS", {"start": v(-10.52, 20.77) * mm, "end": v(-16.37, 20.77) * mm});
            skLineSegment(sketch, "E89.MirrorCS", {"start": v(-10.52, 20.77) * mm, "end": v(-10.52, 6.87) * mm});
            skLineSegment(sketch, "E90.MirrorCS", {"start": v(-10.52, 6.87) * mm, "end": v(-16.37, 6.87) * mm});
            skSolve(sketch);
        }
        {
            var Q0;
            Q0=makeQuery(id+"F26.imprint","IMPRINT",FACE,{"disambiguationData":[TD([[makeQuery(id+"F26.imprint","IMPRINT",EDGE,{"derivedFrom":sQuery(id+"F26.wireOp",EDGE,"E86.bottom")}),-1.0]])]});
            var Q1;
            Q1=makeQuery(id+"F26.imprint","IMPRINT",FACE,{"disambiguationData":[TD([[makeQuery(id+"F26.imprint","IMPRINT",EDGE,{"derivedFrom":sQuery(id+"F26.wireOp",EDGE,"E87.MirrorCS")}),1.0]])]});
            extrude(context, id + "F27", {"entities" : qUnion([Q0, Q1]), "operationType" : NewBodyOperationType.REMOVE, "oppositeDirection" : true, "depth" : 25.4 * mm, "offsetDistance" : 25.4 * mm});
        }
        {
            var Q0;
            Q0=makeQuery(id+"F1.opExtrude","SWEPT_FACE",FACE,{"disambiguationData":[OSD([sQuery(id+"F0.wireOp",EDGE,"E3")])]});
            var sketch = newSketch(context, id + "F28", { "sketchPlane" : qUnion([Q0])});
            skLineSegment(sketch, "E91.bottom", {"start": v(4.32, 22.13) * mm, "end": v(9.48, 22.13) * mm});
            skLineSegment(sketch, "E91.top", {"start": v(4.32, 9.2) * mm, "end": v(9.48, 9.2) * mm});
            skLineSegment(sketch, "E91.left", {"start": v(4.32, 22.13) * mm, "end": v(4.32, 9.2) * mm});
            skLineSegment(sketch, "E91.right", {"start": v(9.48, 22.13) * mm, "end": v(9.48, 9.2) * mm});
            skLineSegment(sketch, "E92.MirrorCS", {"start": v(11.14, 22.13) * mm, "end": v(11.14, 9.2) * mm});
            skLineSegment(sketch, "E93.MirrorCS", {"start": v(16.3, 22.13) * mm, "end": v(11.14, 22.13) * mm});
            skLineSegment(sketch, "E94.MirrorCS", {"start": v(16.3, 22.13) * mm, "end": v(16.3, 9.2) * mm});
            skLineSegment(sketch, "E95.MirrorCS", {"start": v(16.3, 9.2) * mm, "end": v(11.14, 9.2) * mm});
            skSolve(sketch);
        }
        {
            var Q0;
            Q0=makeQuery(id+"F28.imprint","IMPRINT",FACE,{"disambiguationData":[TD([[makeQuery(id+"F28.imprint","IMPRINT",EDGE,{"derivedFrom":sQuery(id+"F28.wireOp",EDGE,"E91.bottom")}),-1.0]])]});
            var Q1;
            Q1=makeQuery(id+"F28.imprint","IMPRINT",FACE,{"disambiguationData":[TD([[makeQuery(id+"F28.imprint","IMPRINT",EDGE,{"derivedFrom":sQuery(id+"F28.wireOp",EDGE,"E92.MirrorCS")}),1.0]])]});
            extrude(context, id + "F29", {"entities" : qUnion([Q0, Q1]), "operationType" : NewBodyOperationType.REMOVE, "oppositeDirection" : true, "depth" : 25.4 * mm, "offsetDistance" : 25.4 * mm});
        }
        {
            var Q0;
            Q0=makeQuery(id+"F1.opExtrude","SWEPT_FACE",FACE,{"disambiguationData":[OSD([sQuery(id+"F0.wireOp",EDGE,"E13")])]});
            var sketch = newSketch(context, id + "F30", { "sketchPlane" : qUnion([Q0])});
            skLineSegment(sketch, "E96.bottom", {"start": v(32.92, 19.84) * mm, "end": v(42.28, 19.84) * mm});
            skLineSegment(sketch, "E96.top", {"start": v(32.92, 6.54) * mm, "end": v(42.28, 6.54) * mm});
            skLineSegment(sketch, "E96.left", {"start": v(32.92, 19.84) * mm, "end": v(32.92, 6.54) * mm});
            skLineSegment(sketch, "E96.right", {"start": v(42.28, 19.84) * mm, "end": v(42.28, 6.54) * mm});
            skSolve(sketch);
        }
        {
            var Q0;
            Q0 = qSketchRegion(id + "F30", true);
            extrude(context, id + "F31", {"entities" : qUnion([Q0]), "operationType" : NewBodyOperationType.REMOVE, "oppositeDirection" : true, "depth" : 25.4 * mm, "offsetDistance" : 25.4 * mm});
        }
        {
            var Q0;
            Q0=makeQuery(id+"F1.opExtrude","SWEPT_FACE",FACE,{"disambiguationData":[OSD([sQuery(id+"F0.wireOp",EDGE,"E8")])]});
            var sketch = newSketch(context, id + "F32", { "sketchPlane" : qUnion([Q0])});
            skLineSegment(sketch, "E97.bottom", {"start": v(29.32, 22.35) * mm, "end": v(35.22, 22.35) * mm});
            skLineSegment(sketch, "E97.top", {"start": v(29.32, 7.97) * mm, "end": v(35.22, 7.97) * mm});
            skLineSegment(sketch, "E97.left", {"start": v(29.32, 22.35) * mm, "end": v(29.32, 7.97) * mm});
            skLineSegment(sketch, "E97.right", {"start": v(35.22, 22.35) * mm, "end": v(35.22, 7.97) * mm});
            skSolve(sketch);
        }
        {
            var Q0;
            Q0 = qSketchRegion(id + "F32", true);
            extrude(context, id + "F33", {"entities" : qUnion([Q0]), "operationType" : NewBodyOperationType.REMOVE, "oppositeDirection" : true, "depth" : 25.4 * mm, "offsetDistance" : 25.4 * mm});
        }
        {
            var Q0;
            Q0=makeQuery(id+"F1.opExtrude","SWEPT_FACE",FACE,{"disambiguationData":[OSD([sQuery(id+"F0.wireOp",EDGE,"E12")])]});
            var sketch = newSketch(context, id + "F34", { "sketchPlane" : qUnion([Q0])});
            skLineSegment(sketch, "E98.bottom", {"start": v(10.25, 21.35) * mm, "end": v(18.29, 21.35) * mm});
            skLineSegment(sketch, "E98.top", {"start": v(10.25, 6.28) * mm, "end": v(18.29, 6.28) * mm});
            skLineSegment(sketch, "E98.left", {"start": v(10.25, 21.35) * mm, "end": v(10.25, 6.28) * mm});
            skLineSegment(sketch, "E98.right", {"start": v(18.29, 21.35) * mm, "end": v(18.29, 6.28) * mm});
            skSolve(sketch);
        }
        {
            var Q0;
            Q0 = qSketchRegion(id + "F34", true);
            extrude(context, id + "F35", {"entities" : qUnion([Q0]), "operationType" : NewBodyOperationType.REMOVE, "oppositeDirection" : true, "depth" : 25.4 * mm, "offsetDistance" : 25.4 * mm});
        }
        {
            var Q0;
            Q0=makeQuery(id+"F1.opExtrude","SWEPT_FACE",FACE,{"disambiguationData":[OSD([sQuery(id+"F0.wireOp",EDGE,"E15")])]});
            var sketch = newSketch(context, id + "F36", { "sketchPlane" : qUnion([Q0])});
            skLineSegment(sketch, "E99.bottom", {"start": v(-40.15, 21.22) * mm, "end": v(-29.87, 21.22) * mm});
            skLineSegment(sketch, "E99.top", {"start": v(-40.15, 5.68) * mm, "end": v(-29.87, 5.68) * mm});
            skLineSegment(sketch, "E99.left", {"start": v(-40.15, 21.22) * mm, "end": v(-40.15, 5.68) * mm});
            skLineSegment(sketch, "E99.right", {"start": v(-29.87, 21.22) * mm, "end": v(-29.87, 5.68) * mm});
            skSolve(sketch);
        }
        {
            var Q0;
            Q0 = qSketchRegion(id + "F36", true);
            extrude(context, id + "F37", {"entities" : qUnion([Q0]), "operationType" : NewBodyOperationType.REMOVE, "oppositeDirection" : true, "depth" : 25.4 * mm, "offsetDistance" : 25.4 * mm});
        }
        {
            var Q0;
            Q0=makeQuery(id+"F1.opExtrude","SWEPT_FACE",FACE,{"disambiguationData":[OSD([sQuery(id+"F0.wireOp",EDGE,"E11")])]});
            var sketch = newSketch(context, id + "F38", { "sketchPlane" : qUnion([Q0])});
            skLineSegment(sketch, "E100.bottom", {"start": v(-2.56, 21.64) * mm, "end": v(2.96, 21.64) * mm});
            skLineSegment(sketch, "E100.top", {"start": v(-2.56, 10.75) * mm, "end": v(2.96, 10.75) * mm});
            skLineSegment(sketch, "E100.left", {"start": v(-2.56, 21.64) * mm, "end": v(-2.56, 10.75) * mm});
            skLineSegment(sketch, "E100.right", {"start": v(2.96, 21.64) * mm, "end": v(2.96, 10.75) * mm});
            skSolve(sketch);
        }
        {
            var Q0;
            Q0 = qSketchRegion(id + "F38", true);
            extrude(context, id + "F39", {"entities" : qUnion([Q0]), "operationType" : NewBodyOperationType.REMOVE, "oppositeDirection" : true, "depth" : 25.4 * mm, "offsetDistance" : 25.4 * mm});
        }
        {
            var Q0;
            {var subQ0=sQuery(id+"F0.wireOp",EDGE,"E55");var subQ1=sQuery(id+"F0.wireOp",EDGE,"E42");var subQ2=sQuery(id+"F0.wireOp",EDGE,"E49");var subQ3=sQuery(id+"F0.wireOp",EDGE,"E26");var subQ4=sQuery(id+"F0.wireOp",EDGE,"E47");var subQ5=sQuery(id+"F0.wireOp",EDGE,"E5");var subQ6=sQuery(id+"F0.wireOp",EDGE,"E46");var subQ7=sQuery(id+"F0.wireOp",EDGE,"E36");var subQ8=sQuery(id+"F0.wireOp",EDGE,"E34");var subQ9=sQuery(id+"F0.wireOp",EDGE,"E53");var subQ10=sQuery(id+"F0.wireOp",EDGE,"E40");var subQ11=sQuery(id+"F0.wireOp",EDGE,"E38");var subQ12=makeQuery(id+"F3.opExtrude","CAP_FACE",FACE,{"disambiguationData":[OSD([sQuery(id+"F2.wireOp",EDGE,"E59.bottom"),sQuery(id+"F2.wireOp",EDGE,"E59.top"),sQuery(id+"F2.wireOp",EDGE,"E59.left"),sQuery(id+"F2.wireOp",EDGE,"E59.right")])],"isStart":true});var subQ13=sQuery(id+"F16.wireOp",EDGE,"E82");var subQ14=sQuery(id+"F12.wireOp",EDGE,"E79.bottom");var subQ16=sQuery(id+"F12.wireOp",EDGE,"E79.top");var subQ18=makeQuery(id+"F1.opExtrude","SWEPT_FACE",FACE,{"disambiguationData":[OSD([sQuery(id+"F0.wireOp",EDGE,"E10")])]});var subQ20=sQuery(id+"F12.wireOp",EDGE,"E79.right");var subQ21=sQuery(id+"F14.wireOp",EDGE,"E80.top");var subQ23=sQuery(id+"F14.wireOp",EDGE,"E80.bottom");var subQ25=makeQuery(id+"F1.opExtrude","SWEPT_FACE",FACE,{"disambiguationData":[OSD([sQuery(id+"F0.wireOp",EDGE,"E11")])]});var subQ26=makeQuery(id+"F15.boolean.opBoolean","MERGE",FACE,{"derivedFrom":[makeQuery(id+"F3.boolean.opBoolean","SPLIT",FACE,{"disambiguationData":[TD([subQ18])],"derivedFrom":subQ12}),makeQuery(id+"F13.boolean.opBoolean","COPY",FACE,{"derivedFrom":makeQuery(id+"F13.opExtrude","CAP_FACE",FACE,{"disambiguationData":[OSD([subQ14,subQ16,sQuery(id+"F12.wireOp",EDGE,"E79.left"),subQ20])],"isStart":false})}),makeQuery(id+"F15.opExtrude","CAP_FACE",FACE,{"disambiguationData":[OSD([subQ23,subQ21,sQuery(id+"F14.wireOp",EDGE,"E80.left"),sQuery(id+"F14.wireOp",EDGE,"E80.right")])],"isStart":false})]});Q0=makeQuery(id+"F25.boolean.opBoolean","MERGE",FACE,{"derivedFrom":[makeQuery(id+"F24.boolean.opBoolean","MERGE",FACE,{"derivedFrom":[makeQuery(id+"F3.boolean.opBoolean","SPLIT",FACE,{"disambiguationData":[TD([makeQuery(id+"F1.opExtrude","SWEPT_FACE",FACE,{"disambiguationData":[OSD([sQuery(id+"F0.wireOp",EDGE,"E7")])]})])],"derivedFrom":subQ12}),makeQuery(id+"F3.boolean.opBoolean","SPLIT",FACE,{"disambiguationData":[TD([makeQuery(id+"F1.opExtrude","SWEPT_FACE",FACE,{"disambiguationData":[OSD([sQuery(id+"F0.wireOp",EDGE,"E12")])]})])],"derivedFrom":subQ12}),makeQuery(id+"F23.boolean.opBoolean","MERGE",FACE,{"derivedFrom":[makeQuery(id+"F3.boolean.opBoolean","SPLIT",FACE,{"disambiguationData":[TD([makeQuery(id+"F1.opExtrude","SWEPT_FACE",FACE,{"disambiguationData":[OSD([sQuery(id+"F0.wireOp",EDGE,"E2")])]})])],"derivedFrom":subQ12}),makeQuery(id+"F22.boolean.opBoolean","MERGE",FACE,{"derivedFrom":[makeQuery(id+"F21.boolean.opBoolean","MERGE",FACE,{"derivedFrom":[makeQuery(id+"F19.boolean.opBoolean","MERGE",FACE,{"derivedFrom":[makeQuery(id+"F17.boolean.opBoolean","SPLIT",FACE,{"disambiguationData":[TD([subQ25])],"derivedFrom":subQ26}),makeQuery(id+"F17.boolean.opBoolean","SPLIT",FACE,{"disambiguationData":[TD([makeQuery(id+"F13.boolean.opBoolean","COPY",FACE,{"derivedFrom":makeQuery(id+"F13.opExtrude","SWEPT_FACE",FACE,{"disambiguationData":[OSD([subQ20])]})})])],"derivedFrom":subQ26}),makeQuery(id+"F19.opExtrude","SWEPT_FACE",FACE,{"disambiguationData":[OSD([subQ13])]})]}),makeQuery(id+"F20.boolean.opBoolean","MERGE",FACE,{"derivedFrom":[makeQuery(id+"F3.boolean.opBoolean","SPLIT",FACE,{"disambiguationData":[TD([makeQuery(id+"F1.opExtrude","SWEPT_FACE",FACE,{"disambiguationData":[OSD([sQuery(id+"F0.wireOp",EDGE,"E1")])]})])],"derivedFrom":subQ12}),makeQuery(id+"F3.boolean.opBoolean","SPLIT",FACE,{"disambiguationData":[TD([makeQuery(id+"F1.opExtrude","SWEPT_FACE",FACE,{"disambiguationData":[OSD([sQuery(id+"F0.wireOp",EDGE,"E33")])]})])],"derivedFrom":subQ12}),makeQuery(id+"F20.opExtrude","SWEPT_FACE",FACE,{"disambiguationData":[OSD([subQ11,subQ10,subQ9])]})]}),makeQuery(id+"F21.opExtrude","SWEPT_FACE",FACE,{"disambiguationData":[OSD([sQuery(id+"F0.wireOp",EDGE,"E21")])]})]}),makeQuery(id+"F22.opExtrude","SWEPT_FACE",FACE,{"disambiguationData":[OSD([subQ8,subQ7,subQ6])]})]}),makeQuery(id+"F23.opExtrude","SWEPT_FACE",FACE,{"disambiguationData":[OSD([subQ5,subQ4])]})]}),makeQuery(id+"F24.opExtrude","SWEPT_FACE",FACE,{"disambiguationData":[OSD([subQ3,subQ2])]})]}),makeQuery(id+"F25.opExtrude","SWEPT_FACE",FACE,{"disambiguationData":[OSD([subQ1,subQ0])]})]});}
            var sketch = newSketch(context, id + "F40", { "sketchPlane" : qUnion([Q0])});
            skLineSegment(sketch, "E101.bottom", {"start": v(15.94, 36.76) * mm, "end": v(30.27, 36.76) * mm});
            skLineSegment(sketch, "E101.top", {"start": v(15.94, 30.65) * mm, "end": v(30.27, 30.65) * mm});
            skLineSegment(sketch, "E101.left", {"start": v(15.94, 36.76) * mm, "end": v(15.94, 30.65) * mm});
            skLineSegment(sketch, "E101.right", {"start": v(30.27, 36.76) * mm, "end": v(30.27, 30.65) * mm});
            skLineSegment(sketch, "E102.bottom", {"start": v(45.54, 14.8) * mm, "end": v(59.86, 14.8) * mm});
            skLineSegment(sketch, "E102.top", {"start": v(45.54, 9.07) * mm, "end": v(59.86, 9.07) * mm});
            skLineSegment(sketch, "E102.left", {"start": v(45.54, 14.8) * mm, "end": v(45.54, 9.07) * mm});
            skLineSegment(sketch, "E102.right", {"start": v(59.86, 14.8) * mm, "end": v(59.86, 9.07) * mm});
            skSolve(sketch);
        }
        {
            var Q0;
            Q0 = qSketchRegion(id + "F40", true);
            extrude(context, id + "F41", {"entities" : qUnion([Q0]), "operationType" : NewBodyOperationType.ADD, "depth" : 6.35 * mm, "offsetDistance" : 25.4 * mm});
        }
        {
            var Q0;
            Q0=makeQuery(id+"F41.opExtrude","CAP_FACE",FACE,{"disambiguationData":[OSD([sQuery(id+"F40.wireOp",EDGE,"E101.bottom"),sQuery(id+"F40.wireOp",EDGE,"E101.top"),sQuery(id+"F40.wireOp",EDGE,"E101.left"),sQuery(id+"F40.wireOp",EDGE,"E101.right")])],"isStart":false});
            var sketch = newSketch(context, id + "F42", { "sketchPlane" : qUnion([Q0])});
            skLineSegment(sketch, "E103.bottom", {"start": v(17.44, 35.42) * mm, "end": v(19.4, 35.42) * mm});
            skLineSegment(sketch, "E103.top", {"start": v(17.44, 32.68) * mm, "end": v(19.4, 32.68) * mm});
            skLineSegment(sketch, "E103.left", {"start": v(17.44, 35.42) * mm, "end": v(17.44, 32.68) * mm});
            skLineSegment(sketch, "E103.right", {"start": v(19.4, 35.42) * mm, "end": v(19.4, 32.68) * mm});
            skLineSegment(sketch, "E104.bottom", {"start": v(57.96, 13.43) * mm, "end": v(55.59, 13.43) * mm});
            skLineSegment(sketch, "E104.top", {"start": v(57.96, 10.41) * mm, "end": v(55.59, 10.41) * mm});
            skLineSegment(sketch, "E104.left", {"start": v(57.96, 13.43) * mm, "end": v(57.96, 10.41) * mm});
            skLineSegment(sketch, "E104.right", {"start": v(55.59, 13.43) * mm, "end": v(55.59, 10.41) * mm});
            skSolve(sketch);
        }
        {
            var Q0;
            Q0 = qSketchRegion(id + "F42", true);
            extrude(context, id + "F43", {"entities" : qUnion([Q0]), "operationType" : NewBodyOperationType.ADD, "depth" : 0.25 * mm, "offsetDistance" : 25.4 * mm});
        }
        {
            var Q0;
            {var subQ0=sQuery(id+"F0.wireOp",EDGE,"E55");var subQ1=sQuery(id+"F0.wireOp",EDGE,"E42");var subQ2=sQuery(id+"F0.wireOp",EDGE,"E49");var subQ3=sQuery(id+"F0.wireOp",EDGE,"E26");var subQ4=sQuery(id+"F0.wireOp",EDGE,"E47");var subQ5=sQuery(id+"F0.wireOp",EDGE,"E5");var subQ6=sQuery(id+"F0.wireOp",EDGE,"E46");var subQ7=sQuery(id+"F0.wireOp",EDGE,"E36");var subQ8=sQuery(id+"F0.wireOp",EDGE,"E34");var subQ9=sQuery(id+"F0.wireOp",EDGE,"E53");var subQ10=sQuery(id+"F0.wireOp",EDGE,"E40");var subQ11=sQuery(id+"F0.wireOp",EDGE,"E38");var subQ12=makeQuery(id+"F3.opExtrude","CAP_FACE",FACE,{"disambiguationData":[OSD([sQuery(id+"F2.wireOp",EDGE,"E59.bottom"),sQuery(id+"F2.wireOp",EDGE,"E59.top"),sQuery(id+"F2.wireOp",EDGE,"E59.left"),sQuery(id+"F2.wireOp",EDGE,"E59.right")])],"isStart":true});var subQ13=sQuery(id+"F16.wireOp",EDGE,"E82");var subQ14=sQuery(id+"F12.wireOp",EDGE,"E79.bottom");var subQ16=sQuery(id+"F12.wireOp",EDGE,"E79.top");var subQ18=makeQuery(id+"F1.opExtrude","SWEPT_FACE",FACE,{"disambiguationData":[OSD([sQuery(id+"F0.wireOp",EDGE,"E10")])]});var subQ20=sQuery(id+"F12.wireOp",EDGE,"E79.right");var subQ21=sQuery(id+"F14.wireOp",EDGE,"E80.top");var subQ23=sQuery(id+"F14.wireOp",EDGE,"E80.bottom");var subQ25=makeQuery(id+"F1.opExtrude","SWEPT_FACE",FACE,{"disambiguationData":[OSD([sQuery(id+"F0.wireOp",EDGE,"E11")])]});var subQ26=makeQuery(id+"F15.boolean.opBoolean","MERGE",FACE,{"derivedFrom":[makeQuery(id+"F3.boolean.opBoolean","SPLIT",FACE,{"disambiguationData":[TD([subQ18])],"derivedFrom":subQ12}),makeQuery(id+"F13.boolean.opBoolean","COPY",FACE,{"derivedFrom":makeQuery(id+"F13.opExtrude","CAP_FACE",FACE,{"disambiguationData":[OSD([subQ14,subQ16,sQuery(id+"F12.wireOp",EDGE,"E79.left"),subQ20])],"isStart":false})}),makeQuery(id+"F15.opExtrude","CAP_FACE",FACE,{"disambiguationData":[OSD([subQ23,subQ21,sQuery(id+"F14.wireOp",EDGE,"E80.left"),sQuery(id+"F14.wireOp",EDGE,"E80.right")])],"isStart":false})]});Q0=makeQuery(id+"F25.boolean.opBoolean","MERGE",FACE,{"derivedFrom":[makeQuery(id+"F24.boolean.opBoolean","MERGE",FACE,{"derivedFrom":[makeQuery(id+"F3.boolean.opBoolean","SPLIT",FACE,{"disambiguationData":[TD([makeQuery(id+"F1.opExtrude","SWEPT_FACE",FACE,{"disambiguationData":[OSD([sQuery(id+"F0.wireOp",EDGE,"E7")])]})])],"derivedFrom":subQ12}),makeQuery(id+"F3.boolean.opBoolean","SPLIT",FACE,{"disambiguationData":[TD([makeQuery(id+"F1.opExtrude","SWEPT_FACE",FACE,{"disambiguationData":[OSD([sQuery(id+"F0.wireOp",EDGE,"E12")])]})])],"derivedFrom":subQ12}),makeQuery(id+"F23.boolean.opBoolean","MERGE",FACE,{"derivedFrom":[makeQuery(id+"F3.boolean.opBoolean","SPLIT",FACE,{"disambiguationData":[TD([makeQuery(id+"F1.opExtrude","SWEPT_FACE",FACE,{"disambiguationData":[OSD([sQuery(id+"F0.wireOp",EDGE,"E2")])]})])],"derivedFrom":subQ12}),makeQuery(id+"F22.boolean.opBoolean","MERGE",FACE,{"derivedFrom":[makeQuery(id+"F21.boolean.opBoolean","MERGE",FACE,{"derivedFrom":[makeQuery(id+"F19.boolean.opBoolean","MERGE",FACE,{"derivedFrom":[makeQuery(id+"F17.boolean.opBoolean","SPLIT",FACE,{"disambiguationData":[TD([subQ25])],"derivedFrom":subQ26}),makeQuery(id+"F17.boolean.opBoolean","SPLIT",FACE,{"disambiguationData":[TD([makeQuery(id+"F13.boolean.opBoolean","COPY",FACE,{"derivedFrom":makeQuery(id+"F13.opExtrude","SWEPT_FACE",FACE,{"disambiguationData":[OSD([subQ20])]})})])],"derivedFrom":subQ26}),makeQuery(id+"F19.opExtrude","SWEPT_FACE",FACE,{"disambiguationData":[OSD([subQ13])]})]}),makeQuery(id+"F20.boolean.opBoolean","MERGE",FACE,{"derivedFrom":[makeQuery(id+"F3.boolean.opBoolean","SPLIT",FACE,{"disambiguationData":[TD([makeQuery(id+"F1.opExtrude","SWEPT_FACE",FACE,{"disambiguationData":[OSD([sQuery(id+"F0.wireOp",EDGE,"E1")])]})])],"derivedFrom":subQ12}),makeQuery(id+"F3.boolean.opBoolean","SPLIT",FACE,{"disambiguationData":[TD([makeQuery(id+"F1.opExtrude","SWEPT_FACE",FACE,{"disambiguationData":[OSD([sQuery(id+"F0.wireOp",EDGE,"E33")])]})])],"derivedFrom":subQ12}),makeQuery(id+"F20.opExtrude","SWEPT_FACE",FACE,{"disambiguationData":[OSD([subQ11,subQ10,subQ9])]})]}),makeQuery(id+"F21.opExtrude","SWEPT_FACE",FACE,{"disambiguationData":[OSD([sQuery(id+"F0.wireOp",EDGE,"E21")])]})]}),makeQuery(id+"F22.opExtrude","SWEPT_FACE",FACE,{"disambiguationData":[OSD([subQ8,subQ7,subQ6])]})]}),makeQuery(id+"F23.opExtrude","SWEPT_FACE",FACE,{"disambiguationData":[OSD([subQ5,subQ4])]})]}),makeQuery(id+"F24.opExtrude","SWEPT_FACE",FACE,{"disambiguationData":[OSD([subQ3,subQ2])]})]}),makeQuery(id+"F25.opExtrude","SWEPT_FACE",FACE,{"disambiguationData":[OSD([subQ1,subQ0])]})]});}
            var sketch = newSketch(context, id + "F44", { "sketchPlane" : qUnion([Q0])});
            skLineSegment(sketch, "E105.bottom", {"start": v(20.32, 19.57) * mm, "end": v(14.81, 19.57) * mm});
            skLineSegment(sketch, "E105.top", {"start": v(20.32, 27.09) * mm, "end": v(14.81, 27.09) * mm});
            skLineSegment(sketch, "E105.left", {"start": v(20.32, 19.57) * mm, "end": v(20.32, 27.09) * mm});
            skLineSegment(sketch, "E105.right", {"start": v(14.81, 19.57) * mm, "end": v(14.81, 27.09) * mm});
            skLineSegment(sketch, "E106.bottom", {"start": v(30.27, 9.3) * mm, "end": v(22.76, 9.3) * mm});
            skLineSegment(sketch, "E106.top", {"start": v(30.27, 14.15) * mm, "end": v(22.76, 14.15) * mm});
            skLineSegment(sketch, "E106.left", {"start": v(30.27, 9.3) * mm, "end": v(30.27, 14.15) * mm});
            skLineSegment(sketch, "E106.right", {"start": v(22.76, 9.3) * mm, "end": v(22.76, 14.15) * mm});
            skSolve(sketch);
        }
        {
            var Q0;
            Q0 = qSketchRegion(id + "F44", true);
            extrude(context, id + "F45", {"entities" : qUnion([Q0]), "operationType" : NewBodyOperationType.ADD, "depth" : 13.97 * mm, "offsetDistance" : 25.4 * mm});
        }
        {
            var Q0;
            {var subQ0=sQuery(id+"F0.wireOp",EDGE,"E55");var subQ1=sQuery(id+"F0.wireOp",EDGE,"E42");var subQ2=sQuery(id+"F0.wireOp",EDGE,"E49");var subQ3=sQuery(id+"F0.wireOp",EDGE,"E26");var subQ4=sQuery(id+"F0.wireOp",EDGE,"E47");var subQ5=sQuery(id+"F0.wireOp",EDGE,"E5");var subQ6=sQuery(id+"F0.wireOp",EDGE,"E46");var subQ7=sQuery(id+"F0.wireOp",EDGE,"E36");var subQ8=sQuery(id+"F0.wireOp",EDGE,"E34");var subQ9=sQuery(id+"F0.wireOp",EDGE,"E53");var subQ10=sQuery(id+"F0.wireOp",EDGE,"E40");var subQ11=sQuery(id+"F0.wireOp",EDGE,"E38");var subQ12=makeQuery(id+"F3.opExtrude","CAP_FACE",FACE,{"disambiguationData":[OSD([sQuery(id+"F2.wireOp",EDGE,"E59.bottom"),sQuery(id+"F2.wireOp",EDGE,"E59.top"),sQuery(id+"F2.wireOp",EDGE,"E59.left"),sQuery(id+"F2.wireOp",EDGE,"E59.right")])],"isStart":true});var subQ13=sQuery(id+"F16.wireOp",EDGE,"E82");var subQ14=sQuery(id+"F12.wireOp",EDGE,"E79.bottom");var subQ16=sQuery(id+"F12.wireOp",EDGE,"E79.top");var subQ18=makeQuery(id+"F1.opExtrude","SWEPT_FACE",FACE,{"disambiguationData":[OSD([sQuery(id+"F0.wireOp",EDGE,"E10")])]});var subQ20=sQuery(id+"F12.wireOp",EDGE,"E79.right");var subQ21=sQuery(id+"F14.wireOp",EDGE,"E80.top");var subQ23=sQuery(id+"F14.wireOp",EDGE,"E80.bottom");var subQ25=makeQuery(id+"F1.opExtrude","SWEPT_FACE",FACE,{"disambiguationData":[OSD([sQuery(id+"F0.wireOp",EDGE,"E11")])]});var subQ26=makeQuery(id+"F15.boolean.opBoolean","MERGE",FACE,{"derivedFrom":[makeQuery(id+"F3.boolean.opBoolean","SPLIT",FACE,{"disambiguationData":[TD([subQ18])],"derivedFrom":subQ12}),makeQuery(id+"F13.boolean.opBoolean","COPY",FACE,{"derivedFrom":makeQuery(id+"F13.opExtrude","CAP_FACE",FACE,{"disambiguationData":[OSD([subQ14,subQ16,sQuery(id+"F12.wireOp",EDGE,"E79.left"),subQ20])],"isStart":false})}),makeQuery(id+"F15.opExtrude","CAP_FACE",FACE,{"disambiguationData":[OSD([subQ23,subQ21,sQuery(id+"F14.wireOp",EDGE,"E80.left"),sQuery(id+"F14.wireOp",EDGE,"E80.right")])],"isStart":false})]});Q0=makeQuery(id+"F25.boolean.opBoolean","MERGE",FACE,{"derivedFrom":[makeQuery(id+"F24.boolean.opBoolean","MERGE",FACE,{"derivedFrom":[makeQuery(id+"F3.boolean.opBoolean","SPLIT",FACE,{"disambiguationData":[TD([makeQuery(id+"F1.opExtrude","SWEPT_FACE",FACE,{"disambiguationData":[OSD([sQuery(id+"F0.wireOp",EDGE,"E7")])]})])],"derivedFrom":subQ12}),makeQuery(id+"F3.boolean.opBoolean","SPLIT",FACE,{"disambiguationData":[TD([makeQuery(id+"F1.opExtrude","SWEPT_FACE",FACE,{"disambiguationData":[OSD([sQuery(id+"F0.wireOp",EDGE,"E12")])]})])],"derivedFrom":subQ12}),makeQuery(id+"F23.boolean.opBoolean","MERGE",FACE,{"derivedFrom":[makeQuery(id+"F3.boolean.opBoolean","SPLIT",FACE,{"disambiguationData":[TD([makeQuery(id+"F1.opExtrude","SWEPT_FACE",FACE,{"disambiguationData":[OSD([sQuery(id+"F0.wireOp",EDGE,"E2")])]})])],"derivedFrom":subQ12}),makeQuery(id+"F22.boolean.opBoolean","MERGE",FACE,{"derivedFrom":[makeQuery(id+"F21.boolean.opBoolean","MERGE",FACE,{"derivedFrom":[makeQuery(id+"F19.boolean.opBoolean","MERGE",FACE,{"derivedFrom":[makeQuery(id+"F17.boolean.opBoolean","SPLIT",FACE,{"disambiguationData":[TD([subQ25])],"derivedFrom":subQ26}),makeQuery(id+"F17.boolean.opBoolean","SPLIT",FACE,{"disambiguationData":[TD([makeQuery(id+"F13.boolean.opBoolean","COPY",FACE,{"derivedFrom":makeQuery(id+"F13.opExtrude","SWEPT_FACE",FACE,{"disambiguationData":[OSD([subQ20])]})})])],"derivedFrom":subQ26}),makeQuery(id+"F19.opExtrude","SWEPT_FACE",FACE,{"disambiguationData":[OSD([subQ13])]})]}),makeQuery(id+"F20.boolean.opBoolean","MERGE",FACE,{"derivedFrom":[makeQuery(id+"F3.boolean.opBoolean","SPLIT",FACE,{"disambiguationData":[TD([makeQuery(id+"F1.opExtrude","SWEPT_FACE",FACE,{"disambiguationData":[OSD([sQuery(id+"F0.wireOp",EDGE,"E1")])]})])],"derivedFrom":subQ12}),makeQuery(id+"F3.boolean.opBoolean","SPLIT",FACE,{"disambiguationData":[TD([makeQuery(id+"F1.opExtrude","SWEPT_FACE",FACE,{"disambiguationData":[OSD([sQuery(id+"F0.wireOp",EDGE,"E33")])]})])],"derivedFrom":subQ12}),makeQuery(id+"F20.opExtrude","SWEPT_FACE",FACE,{"disambiguationData":[OSD([subQ11,subQ10,subQ9])]})]}),makeQuery(id+"F21.opExtrude","SWEPT_FACE",FACE,{"disambiguationData":[OSD([sQuery(id+"F0.wireOp",EDGE,"E21")])]})]}),makeQuery(id+"F22.opExtrude","SWEPT_FACE",FACE,{"disambiguationData":[OSD([subQ8,subQ7,subQ6])]})]}),makeQuery(id+"F23.opExtrude","SWEPT_FACE",FACE,{"disambiguationData":[OSD([subQ5,subQ4])]})]}),makeQuery(id+"F24.opExtrude","SWEPT_FACE",FACE,{"disambiguationData":[OSD([subQ3,subQ2])]})]}),makeQuery(id+"F25.opExtrude","SWEPT_FACE",FACE,{"disambiguationData":[OSD([subQ1,subQ0])]})]});}
            var sketch = newSketch(context, id + "F46", { "sketchPlane" : qUnion([Q0])});
            skLineSegment(sketch, "E107.bottom", {"start": v(40.2, 1.62) * mm, "end": v(51.27, 1.62) * mm});
            skLineSegment(sketch, "E107.top", {"start": v(40.2, -12.5) * mm, "end": v(51.27, -12.5) * mm});
            skLineSegment(sketch, "E107.left", {"start": v(40.2, 1.62) * mm, "end": v(40.2, -12.5) * mm});
            skLineSegment(sketch, "E107.right", {"start": v(51.27, 1.62) * mm, "end": v(51.27, -12.5) * mm});
            skLineSegment(sketch, "E108.bottom", {"start": v(29.31, -8.69) * mm, "end": v(33.51, -8.69) * mm});
            skLineSegment(sketch, "E108.top", {"start": v(29.31, -20.9) * mm, "end": v(33.51, -20.9) * mm});
            skLineSegment(sketch, "E108.left", {"start": v(29.31, -8.69) * mm, "end": v(29.31, -20.9) * mm});
            skLineSegment(sketch, "E108.right", {"start": v(33.51, -8.69) * mm, "end": v(33.51, -20.9) * mm});
            skSolve(sketch);
        }
        {
            var Q0;
            Q0=makeQuery(id+"F46.imprint","IMPRINT",FACE,{"disambiguationData":[TD([[makeQuery(id+"F46.imprint","IMPRINT",EDGE,{"derivedFrom":sQuery(id+"F46.wireOp",EDGE,"E107.bottom")}),-1.0]])]});
            extrude(context, id + "F47", {"entities" : qUnion([Q0]), "operationType" : NewBodyOperationType.ADD, "depth" : 7.11 * mm, "offsetDistance" : 25.4 * mm});
        }
        {
            var Q0;
            Q0=makeQuery(id+"F47.opExtrude","CAP_FACE",FACE,{"disambiguationData":[OSD([sQuery(id+"F46.wireOp",EDGE,"E107.bottom"),sQuery(id+"F46.wireOp",EDGE,"E107.top"),sQuery(id+"F46.wireOp",EDGE,"E107.left"),sQuery(id+"F46.wireOp",EDGE,"E107.right")])],"isStart":false});
            var sketch = newSketch(context, id + "F48", { "sketchPlane" : qUnion([Q0])});
            skLineSegment(sketch, "E109.bottom", {"start": v(41.72, 0) * mm, "end": v(45.16, 0) * mm});
            skLineSegment(sketch, "E109.top", {"start": v(41.72, -2.2) * mm, "end": v(45.16, -2.2) * mm});
            skLineSegment(sketch, "E109.left", {"start": v(41.72, 0) * mm, "end": v(41.72, -2.2) * mm});
            skLineSegment(sketch, "E109.right", {"start": v(45.16, 0) * mm, "end": v(45.16, -2.2) * mm});
            skPoint(sketch, "E110.firstSnap0", {"position": v(45.73, 1.62) * mm});
            skLineSegment(sketch, "E110.bottom", {"start": v(45.73, 0) * mm, "end": v(49.45, 0) * mm});
            skLineSegment(sketch, "E110.top", {"start": v(45.73, -2.2) * mm, "end": v(49.45, -2.2) * mm});
            skLineSegment(sketch, "E110.left", {"start": v(45.73, 0) * mm, "end": v(45.73, -2.2) * mm});
            skLineSegment(sketch, "E110.right", {"start": v(49.45, 0) * mm, "end": v(49.45, -2.2) * mm});
            skSolve(sketch);
        }
        {
            var Q0;
            Q0 = qSketchRegion(id + "F48", true);
            extrude(context, id + "F49", {"entities" : qUnion([Q0]), "operationType" : NewBodyOperationType.ADD, "depth" : 0.66 * mm, "offsetDistance" : 25.4 * mm});
        }
        {
            var Q0;
            {var subQ0=sQuery(id+"F0.wireOp",EDGE,"E55");var subQ1=sQuery(id+"F0.wireOp",EDGE,"E42");var subQ2=sQuery(id+"F0.wireOp",EDGE,"E49");var subQ3=sQuery(id+"F0.wireOp",EDGE,"E26");var subQ4=sQuery(id+"F0.wireOp",EDGE,"E47");var subQ5=sQuery(id+"F0.wireOp",EDGE,"E5");var subQ6=sQuery(id+"F0.wireOp",EDGE,"E46");var subQ7=sQuery(id+"F0.wireOp",EDGE,"E36");var subQ8=sQuery(id+"F0.wireOp",EDGE,"E34");var subQ9=sQuery(id+"F0.wireOp",EDGE,"E53");var subQ10=sQuery(id+"F0.wireOp",EDGE,"E40");var subQ11=sQuery(id+"F0.wireOp",EDGE,"E38");var subQ12=makeQuery(id+"F3.opExtrude","CAP_FACE",FACE,{"disambiguationData":[OSD([sQuery(id+"F2.wireOp",EDGE,"E59.bottom"),sQuery(id+"F2.wireOp",EDGE,"E59.top"),sQuery(id+"F2.wireOp",EDGE,"E59.left"),sQuery(id+"F2.wireOp",EDGE,"E59.right")])],"isStart":true});var subQ13=sQuery(id+"F16.wireOp",EDGE,"E82");var subQ14=sQuery(id+"F12.wireOp",EDGE,"E79.bottom");var subQ16=sQuery(id+"F12.wireOp",EDGE,"E79.top");var subQ18=makeQuery(id+"F1.opExtrude","SWEPT_FACE",FACE,{"disambiguationData":[OSD([sQuery(id+"F0.wireOp",EDGE,"E10")])]});var subQ20=sQuery(id+"F12.wireOp",EDGE,"E79.right");var subQ21=sQuery(id+"F14.wireOp",EDGE,"E80.top");var subQ23=sQuery(id+"F14.wireOp",EDGE,"E80.bottom");var subQ25=makeQuery(id+"F1.opExtrude","SWEPT_FACE",FACE,{"disambiguationData":[OSD([sQuery(id+"F0.wireOp",EDGE,"E11")])]});var subQ26=makeQuery(id+"F15.boolean.opBoolean","MERGE",FACE,{"derivedFrom":[makeQuery(id+"F3.boolean.opBoolean","SPLIT",FACE,{"disambiguationData":[TD([subQ18])],"derivedFrom":subQ12}),makeQuery(id+"F13.boolean.opBoolean","COPY",FACE,{"derivedFrom":makeQuery(id+"F13.opExtrude","CAP_FACE",FACE,{"disambiguationData":[OSD([subQ14,subQ16,sQuery(id+"F12.wireOp",EDGE,"E79.left"),subQ20])],"isStart":false})}),makeQuery(id+"F15.opExtrude","CAP_FACE",FACE,{"disambiguationData":[OSD([subQ23,subQ21,sQuery(id+"F14.wireOp",EDGE,"E80.left"),sQuery(id+"F14.wireOp",EDGE,"E80.right")])],"isStart":false})]});Q0=makeQuery(id+"F25.boolean.opBoolean","MERGE",FACE,{"derivedFrom":[makeQuery(id+"F24.boolean.opBoolean","MERGE",FACE,{"derivedFrom":[makeQuery(id+"F3.boolean.opBoolean","SPLIT",FACE,{"disambiguationData":[TD([makeQuery(id+"F1.opExtrude","SWEPT_FACE",FACE,{"disambiguationData":[OSD([sQuery(id+"F0.wireOp",EDGE,"E7")])]})])],"derivedFrom":subQ12}),makeQuery(id+"F3.boolean.opBoolean","SPLIT",FACE,{"disambiguationData":[TD([makeQuery(id+"F1.opExtrude","SWEPT_FACE",FACE,{"disambiguationData":[OSD([sQuery(id+"F0.wireOp",EDGE,"E12")])]})])],"derivedFrom":subQ12}),makeQuery(id+"F23.boolean.opBoolean","MERGE",FACE,{"derivedFrom":[makeQuery(id+"F3.boolean.opBoolean","SPLIT",FACE,{"disambiguationData":[TD([makeQuery(id+"F1.opExtrude","SWEPT_FACE",FACE,{"disambiguationData":[OSD([sQuery(id+"F0.wireOp",EDGE,"E2")])]})])],"derivedFrom":subQ12}),makeQuery(id+"F22.boolean.opBoolean","MERGE",FACE,{"derivedFrom":[makeQuery(id+"F21.boolean.opBoolean","MERGE",FACE,{"derivedFrom":[makeQuery(id+"F19.boolean.opBoolean","MERGE",FACE,{"derivedFrom":[makeQuery(id+"F17.boolean.opBoolean","SPLIT",FACE,{"disambiguationData":[TD([subQ25])],"derivedFrom":subQ26}),makeQuery(id+"F17.boolean.opBoolean","SPLIT",FACE,{"disambiguationData":[TD([makeQuery(id+"F13.boolean.opBoolean","COPY",FACE,{"derivedFrom":makeQuery(id+"F13.opExtrude","SWEPT_FACE",FACE,{"disambiguationData":[OSD([subQ20])]})})])],"derivedFrom":subQ26}),makeQuery(id+"F19.opExtrude","SWEPT_FACE",FACE,{"disambiguationData":[OSD([subQ13])]})]}),makeQuery(id+"F20.boolean.opBoolean","MERGE",FACE,{"derivedFrom":[makeQuery(id+"F3.boolean.opBoolean","SPLIT",FACE,{"disambiguationData":[TD([makeQuery(id+"F1.opExtrude","SWEPT_FACE",FACE,{"disambiguationData":[OSD([sQuery(id+"F0.wireOp",EDGE,"E1")])]})])],"derivedFrom":subQ12}),makeQuery(id+"F3.boolean.opBoolean","SPLIT",FACE,{"disambiguationData":[TD([makeQuery(id+"F1.opExtrude","SWEPT_FACE",FACE,{"disambiguationData":[OSD([sQuery(id+"F0.wireOp",EDGE,"E33")])]})])],"derivedFrom":subQ12}),makeQuery(id+"F20.opExtrude","SWEPT_FACE",FACE,{"disambiguationData":[OSD([subQ11,subQ10,subQ9])]})]}),makeQuery(id+"F21.opExtrude","SWEPT_FACE",FACE,{"disambiguationData":[OSD([sQuery(id+"F0.wireOp",EDGE,"E21")])]})]}),makeQuery(id+"F22.opExtrude","SWEPT_FACE",FACE,{"disambiguationData":[OSD([subQ8,subQ7,subQ6])]})]}),makeQuery(id+"F23.opExtrude","SWEPT_FACE",FACE,{"disambiguationData":[OSD([subQ5,subQ4])]})]}),makeQuery(id+"F24.opExtrude","SWEPT_FACE",FACE,{"disambiguationData":[OSD([subQ3,subQ2])]})]}),makeQuery(id+"F25.opExtrude","SWEPT_FACE",FACE,{"disambiguationData":[OSD([subQ1,subQ0])]})]});}
            var sketch = newSketch(context, id + "F50", { "sketchPlane" : qUnion([Q0])});
            skLineSegment(sketch, "E111.bottom", {"start": v(28.24, -6.1) * mm, "end": v(30.91, -6.1) * mm});
            skLineSegment(sketch, "E111.top", {"start": v(28.24, -18.18) * mm, "end": v(30.91, -18.18) * mm});
            skLineSegment(sketch, "E111.left", {"start": v(28.24, -6.1) * mm, "end": v(28.24, -18.18) * mm});
            skLineSegment(sketch, "E111.right", {"start": v(30.91, -6.1) * mm, "end": v(30.91, -18.18) * mm});
            skSolve(sketch);
        }
        {
            var Q0;
            Q0 = qSketchRegion(id + "F50", true);
            extrude(context, id + "F51", {"entities" : qUnion([Q0]), "operationType" : NewBodyOperationType.ADD, "depth" : 11.2 * mm, "offsetDistance" : 25.4 * mm});
        }
        {
            var Q0;
            {var subQ0=sQuery(id+"F0.wireOp",EDGE,"E55");var subQ1=sQuery(id+"F0.wireOp",EDGE,"E42");var subQ2=sQuery(id+"F0.wireOp",EDGE,"E49");var subQ3=sQuery(id+"F0.wireOp",EDGE,"E26");var subQ4=sQuery(id+"F0.wireOp",EDGE,"E47");var subQ5=sQuery(id+"F0.wireOp",EDGE,"E5");var subQ6=sQuery(id+"F0.wireOp",EDGE,"E46");var subQ7=sQuery(id+"F0.wireOp",EDGE,"E36");var subQ8=sQuery(id+"F0.wireOp",EDGE,"E34");var subQ9=sQuery(id+"F0.wireOp",EDGE,"E53");var subQ10=sQuery(id+"F0.wireOp",EDGE,"E40");var subQ11=sQuery(id+"F0.wireOp",EDGE,"E38");var subQ12=makeQuery(id+"F3.opExtrude","CAP_FACE",FACE,{"disambiguationData":[OSD([sQuery(id+"F2.wireOp",EDGE,"E59.bottom"),sQuery(id+"F2.wireOp",EDGE,"E59.top"),sQuery(id+"F2.wireOp",EDGE,"E59.left"),sQuery(id+"F2.wireOp",EDGE,"E59.right")])],"isStart":true});var subQ13=sQuery(id+"F16.wireOp",EDGE,"E82");var subQ14=sQuery(id+"F12.wireOp",EDGE,"E79.bottom");var subQ16=sQuery(id+"F12.wireOp",EDGE,"E79.top");var subQ18=makeQuery(id+"F1.opExtrude","SWEPT_FACE",FACE,{"disambiguationData":[OSD([sQuery(id+"F0.wireOp",EDGE,"E10")])]});var subQ20=sQuery(id+"F12.wireOp",EDGE,"E79.right");var subQ21=sQuery(id+"F14.wireOp",EDGE,"E80.top");var subQ23=sQuery(id+"F14.wireOp",EDGE,"E80.bottom");var subQ25=makeQuery(id+"F1.opExtrude","SWEPT_FACE",FACE,{"disambiguationData":[OSD([sQuery(id+"F0.wireOp",EDGE,"E11")])]});var subQ26=makeQuery(id+"F15.boolean.opBoolean","MERGE",FACE,{"derivedFrom":[makeQuery(id+"F3.boolean.opBoolean","SPLIT",FACE,{"disambiguationData":[TD([subQ18])],"derivedFrom":subQ12}),makeQuery(id+"F13.boolean.opBoolean","COPY",FACE,{"derivedFrom":makeQuery(id+"F13.opExtrude","CAP_FACE",FACE,{"disambiguationData":[OSD([subQ14,subQ16,sQuery(id+"F12.wireOp",EDGE,"E79.left"),subQ20])],"isStart":false})}),makeQuery(id+"F15.opExtrude","CAP_FACE",FACE,{"disambiguationData":[OSD([subQ23,subQ21,sQuery(id+"F14.wireOp",EDGE,"E80.left"),sQuery(id+"F14.wireOp",EDGE,"E80.right")])],"isStart":false})]});Q0=makeQuery(id+"F25.boolean.opBoolean","MERGE",FACE,{"derivedFrom":[makeQuery(id+"F24.boolean.opBoolean","MERGE",FACE,{"derivedFrom":[makeQuery(id+"F3.boolean.opBoolean","SPLIT",FACE,{"disambiguationData":[TD([makeQuery(id+"F1.opExtrude","SWEPT_FACE",FACE,{"disambiguationData":[OSD([sQuery(id+"F0.wireOp",EDGE,"E7")])]})])],"derivedFrom":subQ12}),makeQuery(id+"F3.boolean.opBoolean","SPLIT",FACE,{"disambiguationData":[TD([makeQuery(id+"F1.opExtrude","SWEPT_FACE",FACE,{"disambiguationData":[OSD([sQuery(id+"F0.wireOp",EDGE,"E12")])]})])],"derivedFrom":subQ12}),makeQuery(id+"F23.boolean.opBoolean","MERGE",FACE,{"derivedFrom":[makeQuery(id+"F3.boolean.opBoolean","SPLIT",FACE,{"disambiguationData":[TD([makeQuery(id+"F1.opExtrude","SWEPT_FACE",FACE,{"disambiguationData":[OSD([sQuery(id+"F0.wireOp",EDGE,"E2")])]})])],"derivedFrom":subQ12}),makeQuery(id+"F22.boolean.opBoolean","MERGE",FACE,{"derivedFrom":[makeQuery(id+"F21.boolean.opBoolean","MERGE",FACE,{"derivedFrom":[makeQuery(id+"F19.boolean.opBoolean","MERGE",FACE,{"derivedFrom":[makeQuery(id+"F17.boolean.opBoolean","SPLIT",FACE,{"disambiguationData":[TD([subQ25])],"derivedFrom":subQ26}),makeQuery(id+"F17.boolean.opBoolean","SPLIT",FACE,{"disambiguationData":[TD([makeQuery(id+"F13.boolean.opBoolean","COPY",FACE,{"derivedFrom":makeQuery(id+"F13.opExtrude","SWEPT_FACE",FACE,{"disambiguationData":[OSD([subQ20])]})})])],"derivedFrom":subQ26}),makeQuery(id+"F19.opExtrude","SWEPT_FACE",FACE,{"disambiguationData":[OSD([subQ13])]})]}),makeQuery(id+"F20.boolean.opBoolean","MERGE",FACE,{"derivedFrom":[makeQuery(id+"F3.boolean.opBoolean","SPLIT",FACE,{"disambiguationData":[TD([makeQuery(id+"F1.opExtrude","SWEPT_FACE",FACE,{"disambiguationData":[OSD([sQuery(id+"F0.wireOp",EDGE,"E1")])]})])],"derivedFrom":subQ12}),makeQuery(id+"F3.boolean.opBoolean","SPLIT",FACE,{"disambiguationData":[TD([makeQuery(id+"F1.opExtrude","SWEPT_FACE",FACE,{"disambiguationData":[OSD([sQuery(id+"F0.wireOp",EDGE,"E33")])]})])],"derivedFrom":subQ12}),makeQuery(id+"F20.opExtrude","SWEPT_FACE",FACE,{"disambiguationData":[OSD([subQ11,subQ10,subQ9])]})]}),makeQuery(id+"F21.opExtrude","SWEPT_FACE",FACE,{"disambiguationData":[OSD([sQuery(id+"F0.wireOp",EDGE,"E21")])]})]}),makeQuery(id+"F22.opExtrude","SWEPT_FACE",FACE,{"disambiguationData":[OSD([subQ8,subQ7,subQ6])]})]}),makeQuery(id+"F23.opExtrude","SWEPT_FACE",FACE,{"disambiguationData":[OSD([subQ5,subQ4])]})]}),makeQuery(id+"F24.opExtrude","SWEPT_FACE",FACE,{"disambiguationData":[OSD([subQ3,subQ2])]})]}),makeQuery(id+"F25.opExtrude","SWEPT_FACE",FACE,{"disambiguationData":[OSD([subQ1,subQ0])]})]});}
            var sketch = newSketch(context, id + "F52", { "sketchPlane" : qUnion([Q0])});
            skLineSegment(sketch, "E112.bottom", {"start": v(-52.8, 32.15) * mm, "end": v(-44.73, 32.15) * mm});
            skLineSegment(sketch, "E112.top", {"start": v(-52.8, 20.16) * mm, "end": v(-44.73, 20.16) * mm});
            skLineSegment(sketch, "E112.left", {"start": v(-52.8, 32.15) * mm, "end": v(-52.8, 20.16) * mm});
            skLineSegment(sketch, "E112.right", {"start": v(-44.73, 32.15) * mm, "end": v(-44.73, 20.16) * mm});
            skSolve(sketch);
        }
        {
            var Q0;
            Q0 = qSketchRegion(id + "F52", true);
            extrude(context, id + "F53", {"entities" : qUnion([Q0]), "operationType" : NewBodyOperationType.ADD, "depth" : 6.86 * mm, "offsetDistance" : 25.4 * mm});
        }
        {
            var Q0;
            Q0=makeQuery(id+"F53.opExtrude","CAP_FACE",FACE,{"disambiguationData":[OSD([sQuery(id+"F52.wireOp",EDGE,"E112.bottom"),sQuery(id+"F52.wireOp",EDGE,"E112.top"),sQuery(id+"F52.wireOp",EDGE,"E112.left"),sQuery(id+"F52.wireOp",EDGE,"E112.right")])],"isStart":false});
            var sketch = newSketch(context, id + "F54", { "sketchPlane" : qUnion([Q0])});
            skLineSegment(sketch, "E113", {"start": v(-50.52, 20.16) * mm, "end": v(-44.73, 20.16) * mm});
            skLineSegment(sketch, "E114", {"start": v(-49.56, 31.33) * mm, "end": v(-49.56, 20.93) * mm});
            skLineSegment(sketch, "E115", {"start": v(-49.56, 20.93) * mm, "end": v(-44.73, 20.93) * mm});
            skLineSegment(sketch, "E116", {"start": v(-44.73, 20.93) * mm, "end": v(-44.73, 31.33) * mm});
            skLineSegment(sketch, "E117", {"start": v(-44.73, 31.33) * mm, "end": v(-49.56, 31.33) * mm});
            skSolve(sketch);
        }
        {
            var Q0;
            Q0 = qSketchRegion(id + "F54", true);
            extrude(context, id + "F55", {"entities" : qUnion([Q0]), "operationType" : NewBodyOperationType.REMOVE, "oppositeDirection" : true, "depth" : 2.72 * mm, "offsetDistance" : 25.4 * mm});
        }
        {
            var Q0;
            {var subQ0=sQuery(id+"F0.wireOp",EDGE,"E55");var subQ1=sQuery(id+"F0.wireOp",EDGE,"E42");var subQ2=sQuery(id+"F0.wireOp",EDGE,"E49");var subQ3=sQuery(id+"F0.wireOp",EDGE,"E26");var subQ4=sQuery(id+"F0.wireOp",EDGE,"E47");var subQ5=sQuery(id+"F0.wireOp",EDGE,"E5");var subQ6=sQuery(id+"F0.wireOp",EDGE,"E46");var subQ7=sQuery(id+"F0.wireOp",EDGE,"E36");var subQ8=sQuery(id+"F0.wireOp",EDGE,"E34");var subQ9=sQuery(id+"F0.wireOp",EDGE,"E53");var subQ10=sQuery(id+"F0.wireOp",EDGE,"E40");var subQ11=sQuery(id+"F0.wireOp",EDGE,"E38");var subQ12=makeQuery(id+"F3.opExtrude","CAP_FACE",FACE,{"disambiguationData":[OSD([sQuery(id+"F2.wireOp",EDGE,"E59.bottom"),sQuery(id+"F2.wireOp",EDGE,"E59.top"),sQuery(id+"F2.wireOp",EDGE,"E59.left"),sQuery(id+"F2.wireOp",EDGE,"E59.right")])],"isStart":true});var subQ13=sQuery(id+"F16.wireOp",EDGE,"E82");var subQ14=sQuery(id+"F12.wireOp",EDGE,"E79.bottom");var subQ16=sQuery(id+"F12.wireOp",EDGE,"E79.top");var subQ18=makeQuery(id+"F1.opExtrude","SWEPT_FACE",FACE,{"disambiguationData":[OSD([sQuery(id+"F0.wireOp",EDGE,"E10")])]});var subQ20=sQuery(id+"F12.wireOp",EDGE,"E79.right");var subQ21=sQuery(id+"F14.wireOp",EDGE,"E80.top");var subQ23=sQuery(id+"F14.wireOp",EDGE,"E80.bottom");var subQ25=makeQuery(id+"F1.opExtrude","SWEPT_FACE",FACE,{"disambiguationData":[OSD([sQuery(id+"F0.wireOp",EDGE,"E11")])]});var subQ26=makeQuery(id+"F15.boolean.opBoolean","MERGE",FACE,{"derivedFrom":[makeQuery(id+"F3.boolean.opBoolean","SPLIT",FACE,{"disambiguationData":[TD([subQ18])],"derivedFrom":subQ12}),makeQuery(id+"F13.boolean.opBoolean","COPY",FACE,{"derivedFrom":makeQuery(id+"F13.opExtrude","CAP_FACE",FACE,{"disambiguationData":[OSD([subQ14,subQ16,sQuery(id+"F12.wireOp",EDGE,"E79.left"),subQ20])],"isStart":false})}),makeQuery(id+"F15.opExtrude","CAP_FACE",FACE,{"disambiguationData":[OSD([subQ23,subQ21,sQuery(id+"F14.wireOp",EDGE,"E80.left"),sQuery(id+"F14.wireOp",EDGE,"E80.right")])],"isStart":false})]});Q0=makeQuery(id+"F25.boolean.opBoolean","MERGE",FACE,{"derivedFrom":[makeQuery(id+"F24.boolean.opBoolean","MERGE",FACE,{"derivedFrom":[makeQuery(id+"F3.boolean.opBoolean","SPLIT",FACE,{"disambiguationData":[TD([makeQuery(id+"F1.opExtrude","SWEPT_FACE",FACE,{"disambiguationData":[OSD([sQuery(id+"F0.wireOp",EDGE,"E7")])]})])],"derivedFrom":subQ12}),makeQuery(id+"F3.boolean.opBoolean","SPLIT",FACE,{"disambiguationData":[TD([makeQuery(id+"F1.opExtrude","SWEPT_FACE",FACE,{"disambiguationData":[OSD([sQuery(id+"F0.wireOp",EDGE,"E12")])]})])],"derivedFrom":subQ12}),makeQuery(id+"F23.boolean.opBoolean","MERGE",FACE,{"derivedFrom":[makeQuery(id+"F3.boolean.opBoolean","SPLIT",FACE,{"disambiguationData":[TD([makeQuery(id+"F1.opExtrude","SWEPT_FACE",FACE,{"disambiguationData":[OSD([sQuery(id+"F0.wireOp",EDGE,"E2")])]})])],"derivedFrom":subQ12}),makeQuery(id+"F22.boolean.opBoolean","MERGE",FACE,{"derivedFrom":[makeQuery(id+"F21.boolean.opBoolean","MERGE",FACE,{"derivedFrom":[makeQuery(id+"F19.boolean.opBoolean","MERGE",FACE,{"derivedFrom":[makeQuery(id+"F17.boolean.opBoolean","SPLIT",FACE,{"disambiguationData":[TD([subQ25])],"derivedFrom":subQ26}),makeQuery(id+"F17.boolean.opBoolean","SPLIT",FACE,{"disambiguationData":[TD([makeQuery(id+"F13.boolean.opBoolean","COPY",FACE,{"derivedFrom":makeQuery(id+"F13.opExtrude","SWEPT_FACE",FACE,{"disambiguationData":[OSD([subQ20])]})})])],"derivedFrom":subQ26}),makeQuery(id+"F19.opExtrude","SWEPT_FACE",FACE,{"disambiguationData":[OSD([subQ13])]})]}),makeQuery(id+"F20.boolean.opBoolean","MERGE",FACE,{"derivedFrom":[makeQuery(id+"F3.boolean.opBoolean","SPLIT",FACE,{"disambiguationData":[TD([makeQuery(id+"F1.opExtrude","SWEPT_FACE",FACE,{"disambiguationData":[OSD([sQuery(id+"F0.wireOp",EDGE,"E1")])]})])],"derivedFrom":subQ12}),makeQuery(id+"F3.boolean.opBoolean","SPLIT",FACE,{"disambiguationData":[TD([makeQuery(id+"F1.opExtrude","SWEPT_FACE",FACE,{"disambiguationData":[OSD([sQuery(id+"F0.wireOp",EDGE,"E33")])]})])],"derivedFrom":subQ12}),makeQuery(id+"F20.opExtrude","SWEPT_FACE",FACE,{"disambiguationData":[OSD([subQ11,subQ10,subQ9])]})]}),makeQuery(id+"F21.opExtrude","SWEPT_FACE",FACE,{"disambiguationData":[OSD([sQuery(id+"F0.wireOp",EDGE,"E21")])]})]}),makeQuery(id+"F22.opExtrude","SWEPT_FACE",FACE,{"disambiguationData":[OSD([subQ8,subQ7,subQ6])]})]}),makeQuery(id+"F23.opExtrude","SWEPT_FACE",FACE,{"disambiguationData":[OSD([subQ5,subQ4])]})]}),makeQuery(id+"F24.opExtrude","SWEPT_FACE",FACE,{"disambiguationData":[OSD([subQ3,subQ2])]})]}),makeQuery(id+"F25.opExtrude","SWEPT_FACE",FACE,{"disambiguationData":[OSD([subQ1,subQ0])]})]});}
            var sketch = newSketch(context, id + "F56", { "sketchPlane" : qUnion([Q0])});
            skLineSegment(sketch, "E118.bottom", {"start": v(-18.56, 28.46) * mm, "end": v(-16.68, 28.46) * mm});
            skLineSegment(sketch, "E118.top", {"start": v(-18.56, 23.22) * mm, "end": v(-16.68, 23.22) * mm});
            skLineSegment(sketch, "E118.left", {"start": v(-18.56, 28.46) * mm, "end": v(-18.56, 23.22) * mm});
            skLineSegment(sketch, "E118.right", {"start": v(-16.68, 28.46) * mm, "end": v(-16.68, 23.22) * mm});
            skSolve(sketch);
        }
        {
            var Q0;
            Q0 = qSketchRegion(id + "F56", true);
            extrude(context, id + "F57", {"entities" : qUnion([Q0]), "operationType" : NewBodyOperationType.ADD, "depth" : 3.38 * mm, "offsetDistance" : 25.4 * mm});
        }
        {
            var Q0;
            Q0=makeQuery(id+"F57.opExtrude","CAP_FACE",FACE,{"disambiguationData":[OSD([sQuery(id+"F56.wireOp",EDGE,"E118.bottom"),sQuery(id+"F56.wireOp",EDGE,"E118.top"),sQuery(id+"F56.wireOp",EDGE,"E118.left"),sQuery(id+"F56.wireOp",EDGE,"E118.right")])],"isStart":false});
            var sketch = newSketch(context, id + "F58", { "sketchPlane" : qUnion([Q0])});
            skLineSegment(sketch, "E119.bottom", {"start": v(-18.06, 27.71) * mm, "end": v(-17.12, 27.71) * mm});
            skLineSegment(sketch, "E119.top", {"start": v(-18.06, 23.84) * mm, "end": v(-17.12, 23.84) * mm});
            skLineSegment(sketch, "E119.left", {"start": v(-18.06, 27.71) * mm, "end": v(-18.06, 23.84) * mm});
            skLineSegment(sketch, "E119.right", {"start": v(-17.12, 27.71) * mm, "end": v(-17.12, 23.84) * mm});
            skSolve(sketch);
        }
        {
            var Q0;
            Q0 = qSketchRegion(id + "F58", true);
            extrude(context, id + "F59", {"entities" : qUnion([Q0]), "operationType" : NewBodyOperationType.ADD, "depth" : 3.8 * mm, "offsetDistance" : 25.4 * mm});
        }
        {
            var Q0;
            {var subQ0=sQuery(id+"F0.wireOp",EDGE,"E55");var subQ1=sQuery(id+"F0.wireOp",EDGE,"E42");var subQ2=sQuery(id+"F0.wireOp",EDGE,"E49");var subQ3=sQuery(id+"F0.wireOp",EDGE,"E26");var subQ4=sQuery(id+"F0.wireOp",EDGE,"E47");var subQ5=sQuery(id+"F0.wireOp",EDGE,"E5");var subQ6=sQuery(id+"F0.wireOp",EDGE,"E46");var subQ7=sQuery(id+"F0.wireOp",EDGE,"E36");var subQ8=sQuery(id+"F0.wireOp",EDGE,"E34");var subQ9=sQuery(id+"F0.wireOp",EDGE,"E53");var subQ10=sQuery(id+"F0.wireOp",EDGE,"E40");var subQ11=sQuery(id+"F0.wireOp",EDGE,"E38");var subQ12=makeQuery(id+"F3.opExtrude","CAP_FACE",FACE,{"disambiguationData":[OSD([sQuery(id+"F2.wireOp",EDGE,"E59.bottom"),sQuery(id+"F2.wireOp",EDGE,"E59.top"),sQuery(id+"F2.wireOp",EDGE,"E59.left"),sQuery(id+"F2.wireOp",EDGE,"E59.right")])],"isStart":true});var subQ13=sQuery(id+"F16.wireOp",EDGE,"E82");var subQ14=sQuery(id+"F12.wireOp",EDGE,"E79.bottom");var subQ16=sQuery(id+"F12.wireOp",EDGE,"E79.top");var subQ18=makeQuery(id+"F1.opExtrude","SWEPT_FACE",FACE,{"disambiguationData":[OSD([sQuery(id+"F0.wireOp",EDGE,"E10")])]});var subQ20=sQuery(id+"F12.wireOp",EDGE,"E79.right");var subQ21=sQuery(id+"F14.wireOp",EDGE,"E80.top");var subQ23=sQuery(id+"F14.wireOp",EDGE,"E80.bottom");var subQ25=makeQuery(id+"F1.opExtrude","SWEPT_FACE",FACE,{"disambiguationData":[OSD([sQuery(id+"F0.wireOp",EDGE,"E11")])]});var subQ26=makeQuery(id+"F15.boolean.opBoolean","MERGE",FACE,{"derivedFrom":[makeQuery(id+"F3.boolean.opBoolean","SPLIT",FACE,{"disambiguationData":[TD([subQ18])],"derivedFrom":subQ12}),makeQuery(id+"F13.boolean.opBoolean","COPY",FACE,{"derivedFrom":makeQuery(id+"F13.opExtrude","CAP_FACE",FACE,{"disambiguationData":[OSD([subQ14,subQ16,sQuery(id+"F12.wireOp",EDGE,"E79.left"),subQ20])],"isStart":false})}),makeQuery(id+"F15.opExtrude","CAP_FACE",FACE,{"disambiguationData":[OSD([subQ23,subQ21,sQuery(id+"F14.wireOp",EDGE,"E80.left"),sQuery(id+"F14.wireOp",EDGE,"E80.right")])],"isStart":false})]});Q0=makeQuery(id+"F25.boolean.opBoolean","MERGE",FACE,{"derivedFrom":[makeQuery(id+"F24.boolean.opBoolean","MERGE",FACE,{"derivedFrom":[makeQuery(id+"F3.boolean.opBoolean","SPLIT",FACE,{"disambiguationData":[TD([makeQuery(id+"F1.opExtrude","SWEPT_FACE",FACE,{"disambiguationData":[OSD([sQuery(id+"F0.wireOp",EDGE,"E7")])]})])],"derivedFrom":subQ12}),makeQuery(id+"F3.boolean.opBoolean","SPLIT",FACE,{"disambiguationData":[TD([makeQuery(id+"F1.opExtrude","SWEPT_FACE",FACE,{"disambiguationData":[OSD([sQuery(id+"F0.wireOp",EDGE,"E12")])]})])],"derivedFrom":subQ12}),makeQuery(id+"F23.boolean.opBoolean","MERGE",FACE,{"derivedFrom":[makeQuery(id+"F3.boolean.opBoolean","SPLIT",FACE,{"disambiguationData":[TD([makeQuery(id+"F1.opExtrude","SWEPT_FACE",FACE,{"disambiguationData":[OSD([sQuery(id+"F0.wireOp",EDGE,"E2")])]})])],"derivedFrom":subQ12}),makeQuery(id+"F22.boolean.opBoolean","MERGE",FACE,{"derivedFrom":[makeQuery(id+"F21.boolean.opBoolean","MERGE",FACE,{"derivedFrom":[makeQuery(id+"F19.boolean.opBoolean","MERGE",FACE,{"derivedFrom":[makeQuery(id+"F17.boolean.opBoolean","SPLIT",FACE,{"disambiguationData":[TD([subQ25])],"derivedFrom":subQ26}),makeQuery(id+"F17.boolean.opBoolean","SPLIT",FACE,{"disambiguationData":[TD([makeQuery(id+"F13.boolean.opBoolean","COPY",FACE,{"derivedFrom":makeQuery(id+"F13.opExtrude","SWEPT_FACE",FACE,{"disambiguationData":[OSD([subQ20])]})})])],"derivedFrom":subQ26}),makeQuery(id+"F19.opExtrude","SWEPT_FACE",FACE,{"disambiguationData":[OSD([subQ13])]})]}),makeQuery(id+"F20.boolean.opBoolean","MERGE",FACE,{"derivedFrom":[makeQuery(id+"F3.boolean.opBoolean","SPLIT",FACE,{"disambiguationData":[TD([makeQuery(id+"F1.opExtrude","SWEPT_FACE",FACE,{"disambiguationData":[OSD([sQuery(id+"F0.wireOp",EDGE,"E1")])]})])],"derivedFrom":subQ12}),makeQuery(id+"F3.boolean.opBoolean","SPLIT",FACE,{"disambiguationData":[TD([makeQuery(id+"F1.opExtrude","SWEPT_FACE",FACE,{"disambiguationData":[OSD([sQuery(id+"F0.wireOp",EDGE,"E33")])]})])],"derivedFrom":subQ12}),makeQuery(id+"F20.opExtrude","SWEPT_FACE",FACE,{"disambiguationData":[OSD([subQ11,subQ10,subQ9])]})]}),makeQuery(id+"F21.opExtrude","SWEPT_FACE",FACE,{"disambiguationData":[OSD([sQuery(id+"F0.wireOp",EDGE,"E21")])]})]}),makeQuery(id+"F22.opExtrude","SWEPT_FACE",FACE,{"disambiguationData":[OSD([subQ8,subQ7,subQ6])]})]}),makeQuery(id+"F23.opExtrude","SWEPT_FACE",FACE,{"disambiguationData":[OSD([subQ5,subQ4])]})]}),makeQuery(id+"F24.opExtrude","SWEPT_FACE",FACE,{"disambiguationData":[OSD([subQ3,subQ2])]})]}),makeQuery(id+"F25.opExtrude","SWEPT_FACE",FACE,{"disambiguationData":[OSD([subQ1,subQ0])]})]});}
            var sketch = newSketch(context, id + "F60", { "sketchPlane" : qUnion([Q0])});
            skLineSegment(sketch, "E120.bottom", {"start": v(-50.96, 3.91) * mm, "end": v(-48, 3.91) * mm});
            skLineSegment(sketch, "E120.top", {"start": v(-50.96, 0.73) * mm, "end": v(-48, 0.73) * mm});
            skLineSegment(sketch, "E120.left", {"start": v(-50.96, 3.91) * mm, "end": v(-50.96, 0.73) * mm});
            skLineSegment(sketch, "E120.right", {"start": v(-48, 3.91) * mm, "end": v(-48, 0.73) * mm});
            skSolve(sketch);
        }
        {
            var Q0;
            Q0=makeQuery(id+"F60.imprint","IMPRINT",FACE,{"disambiguationData":[TD([[makeQuery(id+"F60.imprint","IMPRINT",EDGE,{"derivedFrom":sQuery(id+"F60.wireOp",EDGE,"E120.bottom")}),-1.0]])]});
            extrude(context, id + "F61", {"entities" : qUnion([Q0]), "operationType" : NewBodyOperationType.ADD, "depth" : 7.72 * mm, "offsetDistance" : 25.4 * mm});
        }
        {
            var Q0;
            Q0=makeQuery(id+"F61.opExtrude","CAP_FACE",FACE,{"disambiguationData":[OSD([sQuery(id+"F60.wireOp",EDGE,"E120.bottom"),sQuery(id+"F60.wireOp",EDGE,"E120.top"),sQuery(id+"F60.wireOp",EDGE,"E120.left"),sQuery(id+"F60.wireOp",EDGE,"E120.right")])],"isStart":false});
            var sketch = newSketch(context, id + "F62", { "sketchPlane" : qUnion([Q0])});
            skLineSegment(sketch, "E121.bottom", {"start": v(-50.96, 2.32) * mm, "end": v(-48, 2.32) * mm});
            skLineSegment(sketch, "E121.top", {"start": v(-50.96, 0.73) * mm, "end": v(-48, 0.73) * mm});
            skLineSegment(sketch, "E121.left", {"start": v(-50.96, 2.32) * mm, "end": v(-50.96, 0.73) * mm});
            skLineSegment(sketch, "E121.right", {"start": v(-48, 2.32) * mm, "end": v(-48, 0.73) * mm});
            skSolve(sketch);
        }
        {
            var Q0;
            Q0 = qSketchRegion(id + "F62", true);
            extrude(context, id + "F63", {"entities" : qUnion([Q0]), "operationType" : NewBodyOperationType.REMOVE, "oppositeDirection" : true, "depth" : 3.15 * mm, "offsetDistance" : 25.4 * mm});
        }
        {
            var Q0;
            Q0=makeQuery(id+"F63.boolean.opBoolean","COPY",FACE,{"derivedFrom":makeQuery(id+"F63.opExtrude","CAP_FACE",FACE,{"disambiguationData":[OSD([sQuery(id+"F62.wireOp",EDGE,"E121.bottom"),sQuery(id+"F62.wireOp",EDGE,"E121.top"),sQuery(id+"F62.wireOp",EDGE,"E121.left"),sQuery(id+"F62.wireOp",EDGE,"E121.right")])],"isStart":false})});
            var sketch = newSketch(context, id + "F64", { "sketchPlane" : qUnion([Q0])});
            skCircle(sketch, "E122", {"center": v(-49.6, 1.6) * mm, "radius": 0.6 * mm});
            skSolve(sketch);
        }
        {
            var Q0;
            Q0 = qSketchRegion(id + "F64", true);
            extrude(context, id + "F65", {"entities" : qUnion([Q0]), "operationType" : NewBodyOperationType.REMOVE, "oppositeDirection" : true, "depth" : 2.7 * mm, "offsetDistance" : 25.4 * mm});
        }
        {
            var Q0;
            {var subQ0=sQuery(id+"F0.wireOp",EDGE,"E55");var subQ1=sQuery(id+"F0.wireOp",EDGE,"E42");var subQ2=sQuery(id+"F0.wireOp",EDGE,"E49");var subQ3=sQuery(id+"F0.wireOp",EDGE,"E26");var subQ4=sQuery(id+"F0.wireOp",EDGE,"E47");var subQ5=sQuery(id+"F0.wireOp",EDGE,"E5");var subQ6=sQuery(id+"F0.wireOp",EDGE,"E46");var subQ7=sQuery(id+"F0.wireOp",EDGE,"E36");var subQ8=sQuery(id+"F0.wireOp",EDGE,"E34");var subQ9=sQuery(id+"F0.wireOp",EDGE,"E53");var subQ10=sQuery(id+"F0.wireOp",EDGE,"E40");var subQ11=sQuery(id+"F0.wireOp",EDGE,"E38");var subQ12=makeQuery(id+"F3.opExtrude","CAP_FACE",FACE,{"disambiguationData":[OSD([sQuery(id+"F2.wireOp",EDGE,"E59.bottom"),sQuery(id+"F2.wireOp",EDGE,"E59.top"),sQuery(id+"F2.wireOp",EDGE,"E59.left"),sQuery(id+"F2.wireOp",EDGE,"E59.right")])],"isStart":true});var subQ13=sQuery(id+"F16.wireOp",EDGE,"E82");var subQ14=sQuery(id+"F12.wireOp",EDGE,"E79.bottom");var subQ16=sQuery(id+"F12.wireOp",EDGE,"E79.top");var subQ18=makeQuery(id+"F1.opExtrude","SWEPT_FACE",FACE,{"disambiguationData":[OSD([sQuery(id+"F0.wireOp",EDGE,"E10")])]});var subQ20=sQuery(id+"F12.wireOp",EDGE,"E79.right");var subQ21=sQuery(id+"F14.wireOp",EDGE,"E80.top");var subQ23=sQuery(id+"F14.wireOp",EDGE,"E80.bottom");var subQ25=makeQuery(id+"F1.opExtrude","SWEPT_FACE",FACE,{"disambiguationData":[OSD([sQuery(id+"F0.wireOp",EDGE,"E11")])]});var subQ26=makeQuery(id+"F15.boolean.opBoolean","MERGE",FACE,{"derivedFrom":[makeQuery(id+"F3.boolean.opBoolean","SPLIT",FACE,{"disambiguationData":[TD([subQ18])],"derivedFrom":subQ12}),makeQuery(id+"F13.boolean.opBoolean","COPY",FACE,{"derivedFrom":makeQuery(id+"F13.opExtrude","CAP_FACE",FACE,{"disambiguationData":[OSD([subQ14,subQ16,sQuery(id+"F12.wireOp",EDGE,"E79.left"),subQ20])],"isStart":false})}),makeQuery(id+"F15.opExtrude","CAP_FACE",FACE,{"disambiguationData":[OSD([subQ23,subQ21,sQuery(id+"F14.wireOp",EDGE,"E80.left"),sQuery(id+"F14.wireOp",EDGE,"E80.right")])],"isStart":false})]});Q0=makeQuery(id+"F25.boolean.opBoolean","MERGE",FACE,{"derivedFrom":[makeQuery(id+"F24.boolean.opBoolean","MERGE",FACE,{"derivedFrom":[makeQuery(id+"F3.boolean.opBoolean","SPLIT",FACE,{"disambiguationData":[TD([makeQuery(id+"F1.opExtrude","SWEPT_FACE",FACE,{"disambiguationData":[OSD([sQuery(id+"F0.wireOp",EDGE,"E7")])]})])],"derivedFrom":subQ12}),makeQuery(id+"F3.boolean.opBoolean","SPLIT",FACE,{"disambiguationData":[TD([makeQuery(id+"F1.opExtrude","SWEPT_FACE",FACE,{"disambiguationData":[OSD([sQuery(id+"F0.wireOp",EDGE,"E12")])]})])],"derivedFrom":subQ12}),makeQuery(id+"F23.boolean.opBoolean","MERGE",FACE,{"derivedFrom":[makeQuery(id+"F3.boolean.opBoolean","SPLIT",FACE,{"disambiguationData":[TD([makeQuery(id+"F1.opExtrude","SWEPT_FACE",FACE,{"disambiguationData":[OSD([sQuery(id+"F0.wireOp",EDGE,"E2")])]})])],"derivedFrom":subQ12}),makeQuery(id+"F22.boolean.opBoolean","MERGE",FACE,{"derivedFrom":[makeQuery(id+"F21.boolean.opBoolean","MERGE",FACE,{"derivedFrom":[makeQuery(id+"F19.boolean.opBoolean","MERGE",FACE,{"derivedFrom":[makeQuery(id+"F17.boolean.opBoolean","SPLIT",FACE,{"disambiguationData":[TD([subQ25])],"derivedFrom":subQ26}),makeQuery(id+"F17.boolean.opBoolean","SPLIT",FACE,{"disambiguationData":[TD([makeQuery(id+"F13.boolean.opBoolean","COPY",FACE,{"derivedFrom":makeQuery(id+"F13.opExtrude","SWEPT_FACE",FACE,{"disambiguationData":[OSD([subQ20])]})})])],"derivedFrom":subQ26}),makeQuery(id+"F19.opExtrude","SWEPT_FACE",FACE,{"disambiguationData":[OSD([subQ13])]})]}),makeQuery(id+"F20.boolean.opBoolean","MERGE",FACE,{"derivedFrom":[makeQuery(id+"F3.boolean.opBoolean","SPLIT",FACE,{"disambiguationData":[TD([makeQuery(id+"F1.opExtrude","SWEPT_FACE",FACE,{"disambiguationData":[OSD([sQuery(id+"F0.wireOp",EDGE,"E1")])]})])],"derivedFrom":subQ12}),makeQuery(id+"F3.boolean.opBoolean","SPLIT",FACE,{"disambiguationData":[TD([makeQuery(id+"F1.opExtrude","SWEPT_FACE",FACE,{"disambiguationData":[OSD([sQuery(id+"F0.wireOp",EDGE,"E33")])]})])],"derivedFrom":subQ12}),makeQuery(id+"F20.opExtrude","SWEPT_FACE",FACE,{"disambiguationData":[OSD([subQ11,subQ10,subQ9])]})]}),makeQuery(id+"F21.opExtrude","SWEPT_FACE",FACE,{"disambiguationData":[OSD([sQuery(id+"F0.wireOp",EDGE,"E21")])]})]}),makeQuery(id+"F22.opExtrude","SWEPT_FACE",FACE,{"disambiguationData":[OSD([subQ8,subQ7,subQ6])]})]}),makeQuery(id+"F23.opExtrude","SWEPT_FACE",FACE,{"disambiguationData":[OSD([subQ5,subQ4])]})]}),makeQuery(id+"F24.opExtrude","SWEPT_FACE",FACE,{"disambiguationData":[OSD([subQ3,subQ2])]})]}),makeQuery(id+"F25.opExtrude","SWEPT_FACE",FACE,{"disambiguationData":[OSD([subQ1,subQ0])]})]});}
            var sketch = newSketch(context, id + "F66", { "sketchPlane" : qUnion([Q0])});
            skLineSegment(sketch, "E123.bottom", {"start": v(-40.5, 39.77) * mm, "end": v(-27.46, 39.77) * mm});
            skLineSegment(sketch, "E123.top", {"start": v(-40.5, 33.87) * mm, "end": v(-27.46, 33.87) * mm});
            skLineSegment(sketch, "E123.left", {"start": v(-40.5, 39.77) * mm, "end": v(-40.5, 33.87) * mm});
            skLineSegment(sketch, "E123.right", {"start": v(-27.46, 39.77) * mm, "end": v(-27.46, 33.87) * mm});
            skSolve(sketch);
        }
        {
            var Q0;
            Q0 = qSketchRegion(id + "F66", true);
            extrude(context, id + "F67", {"entities" : qUnion([Q0]), "operationType" : NewBodyOperationType.ADD, "depth" : 7.11 * mm, "offsetDistance" : 25.4 * mm});
        }
        {
            var Q0;
            Q0=makeQuery(id+"F67.opExtrude","CAP_FACE",FACE,{"disambiguationData":[OSD([sQuery(id+"F66.wireOp",EDGE,"E123.bottom"),sQuery(id+"F66.wireOp",EDGE,"E123.top"),sQuery(id+"F66.wireOp",EDGE,"E123.left"),sQuery(id+"F66.wireOp",EDGE,"E123.right")])],"isStart":false});
            var sketch = newSketch(context, id + "F68", { "sketchPlane" : qUnion([Q0])});
            skLineSegment(sketch, "E124.bottom", {"start": v(-40.5, 33.87) * mm, "end": v(-27.46, 33.87) * mm});
            skLineSegment(sketch, "E124.top", {"start": v(-40.5, 38.17) * mm, "end": v(-27.46, 38.17) * mm});
            skLineSegment(sketch, "E124.left", {"start": v(-40.5, 33.87) * mm, "end": v(-40.5, 38.17) * mm});
            skLineSegment(sketch, "E124.right", {"start": v(-27.46, 33.87) * mm, "end": v(-27.46, 38.17) * mm});
            skSolve(sketch);
        }
        {
            var Q0;
            Q0 = qSketchRegion(id + "F68", true);
            extrude(context, id + "F69", {"entities" : qUnion([Q0]), "operationType" : NewBodyOperationType.REMOVE, "oppositeDirection" : true, "depth" : 3.5 * mm, "offsetDistance" : 25.4 * mm});
        }
        {
            var Q0;
            Q0=makeQuery(id+"F1.opExtrude","SWEPT_FACE",FACE,{"disambiguationData":[OSD([sQuery(id+"F0.wireOp",EDGE,"E26"),sQuery(id+"F0.wireOp",EDGE,"E49")])]});
            var sketch = newSketch(context, id + "F70", { "sketchPlane" : qUnion([Q0])});
            skLineSegment(sketch, "E125.bottom", {"start": v(-46.63, 10.22) * mm, "end": v(-30.81, 10.22) * mm});
            skLineSegment(sketch, "E125.top", {"start": v(-46.63, 8.89) * mm, "end": v(-30.81, 8.89) * mm});
            skLineSegment(sketch, "E125.left", {"start": v(-46.63, 10.22) * mm, "end": v(-46.63, 8.89) * mm});
            skLineSegment(sketch, "E125.right", {"start": v(-30.81, 10.22) * mm, "end": v(-30.81, 8.89) * mm});
            skSolve(sketch);
        }
        {
            var Q0;
            Q0 = qSketchRegion(id + "F70", true);
            extrude(context, id + "F71", {"entities" : qUnion([Q0]), "operationType" : NewBodyOperationType.ADD, "depth" : 3.56 * mm, "offsetDistance" : 25.4 * mm});
        }
        {
            var Q0;
            {var subQ0=sQuery(id+"F0.wireOp",EDGE,"E55");var subQ1=sQuery(id+"F0.wireOp",EDGE,"E42");var subQ2=sQuery(id+"F0.wireOp",EDGE,"E49");var subQ3=sQuery(id+"F0.wireOp",EDGE,"E26");var subQ4=sQuery(id+"F0.wireOp",EDGE,"E47");var subQ5=sQuery(id+"F0.wireOp",EDGE,"E5");var subQ6=sQuery(id+"F0.wireOp",EDGE,"E46");var subQ7=sQuery(id+"F0.wireOp",EDGE,"E36");var subQ8=sQuery(id+"F0.wireOp",EDGE,"E34");var subQ9=sQuery(id+"F0.wireOp",EDGE,"E53");var subQ10=sQuery(id+"F0.wireOp",EDGE,"E40");var subQ11=sQuery(id+"F0.wireOp",EDGE,"E38");var subQ12=makeQuery(id+"F3.opExtrude","CAP_FACE",FACE,{"disambiguationData":[OSD([sQuery(id+"F2.wireOp",EDGE,"E59.bottom"),sQuery(id+"F2.wireOp",EDGE,"E59.top"),sQuery(id+"F2.wireOp",EDGE,"E59.left"),sQuery(id+"F2.wireOp",EDGE,"E59.right")])],"isStart":true});var subQ13=sQuery(id+"F16.wireOp",EDGE,"E82");var subQ14=sQuery(id+"F12.wireOp",EDGE,"E79.bottom");var subQ16=sQuery(id+"F12.wireOp",EDGE,"E79.top");var subQ18=makeQuery(id+"F1.opExtrude","SWEPT_FACE",FACE,{"disambiguationData":[OSD([sQuery(id+"F0.wireOp",EDGE,"E10")])]});var subQ20=sQuery(id+"F12.wireOp",EDGE,"E79.right");var subQ21=sQuery(id+"F14.wireOp",EDGE,"E80.top");var subQ23=sQuery(id+"F14.wireOp",EDGE,"E80.bottom");var subQ25=makeQuery(id+"F1.opExtrude","SWEPT_FACE",FACE,{"disambiguationData":[OSD([sQuery(id+"F0.wireOp",EDGE,"E11")])]});var subQ26=makeQuery(id+"F15.boolean.opBoolean","MERGE",FACE,{"derivedFrom":[makeQuery(id+"F3.boolean.opBoolean","SPLIT",FACE,{"disambiguationData":[TD([subQ18])],"derivedFrom":subQ12}),makeQuery(id+"F13.boolean.opBoolean","COPY",FACE,{"derivedFrom":makeQuery(id+"F13.opExtrude","CAP_FACE",FACE,{"disambiguationData":[OSD([subQ14,subQ16,sQuery(id+"F12.wireOp",EDGE,"E79.left"),subQ20])],"isStart":false})}),makeQuery(id+"F15.opExtrude","CAP_FACE",FACE,{"disambiguationData":[OSD([subQ23,subQ21,sQuery(id+"F14.wireOp",EDGE,"E80.left"),sQuery(id+"F14.wireOp",EDGE,"E80.right")])],"isStart":false})]});Q0=makeQuery(id+"F25.boolean.opBoolean","MERGE",FACE,{"derivedFrom":[makeQuery(id+"F24.boolean.opBoolean","MERGE",FACE,{"derivedFrom":[makeQuery(id+"F3.boolean.opBoolean","SPLIT",FACE,{"disambiguationData":[TD([makeQuery(id+"F1.opExtrude","SWEPT_FACE",FACE,{"disambiguationData":[OSD([sQuery(id+"F0.wireOp",EDGE,"E7")])]})])],"derivedFrom":subQ12}),makeQuery(id+"F3.boolean.opBoolean","SPLIT",FACE,{"disambiguationData":[TD([makeQuery(id+"F1.opExtrude","SWEPT_FACE",FACE,{"disambiguationData":[OSD([sQuery(id+"F0.wireOp",EDGE,"E12")])]})])],"derivedFrom":subQ12}),makeQuery(id+"F23.boolean.opBoolean","MERGE",FACE,{"derivedFrom":[makeQuery(id+"F3.boolean.opBoolean","SPLIT",FACE,{"disambiguationData":[TD([makeQuery(id+"F1.opExtrude","SWEPT_FACE",FACE,{"disambiguationData":[OSD([sQuery(id+"F0.wireOp",EDGE,"E2")])]})])],"derivedFrom":subQ12}),makeQuery(id+"F22.boolean.opBoolean","MERGE",FACE,{"derivedFrom":[makeQuery(id+"F21.boolean.opBoolean","MERGE",FACE,{"derivedFrom":[makeQuery(id+"F19.boolean.opBoolean","MERGE",FACE,{"derivedFrom":[makeQuery(id+"F17.boolean.opBoolean","SPLIT",FACE,{"disambiguationData":[TD([subQ25])],"derivedFrom":subQ26}),makeQuery(id+"F17.boolean.opBoolean","SPLIT",FACE,{"disambiguationData":[TD([makeQuery(id+"F13.boolean.opBoolean","COPY",FACE,{"derivedFrom":makeQuery(id+"F13.opExtrude","SWEPT_FACE",FACE,{"disambiguationData":[OSD([subQ20])]})})])],"derivedFrom":subQ26}),makeQuery(id+"F19.opExtrude","SWEPT_FACE",FACE,{"disambiguationData":[OSD([subQ13])]})]}),makeQuery(id+"F20.boolean.opBoolean","MERGE",FACE,{"derivedFrom":[makeQuery(id+"F3.boolean.opBoolean","SPLIT",FACE,{"disambiguationData":[TD([makeQuery(id+"F1.opExtrude","SWEPT_FACE",FACE,{"disambiguationData":[OSD([sQuery(id+"F0.wireOp",EDGE,"E1")])]})])],"derivedFrom":subQ12}),makeQuery(id+"F3.boolean.opBoolean","SPLIT",FACE,{"disambiguationData":[TD([makeQuery(id+"F1.opExtrude","SWEPT_FACE",FACE,{"disambiguationData":[OSD([sQuery(id+"F0.wireOp",EDGE,"E33")])]})])],"derivedFrom":subQ12}),makeQuery(id+"F20.opExtrude","SWEPT_FACE",FACE,{"disambiguationData":[OSD([subQ11,subQ10,subQ9])]})]}),makeQuery(id+"F21.opExtrude","SWEPT_FACE",FACE,{"disambiguationData":[OSD([sQuery(id+"F0.wireOp",EDGE,"E21")])]})]}),makeQuery(id+"F22.opExtrude","SWEPT_FACE",FACE,{"disambiguationData":[OSD([subQ8,subQ7,subQ6])]})]}),makeQuery(id+"F23.opExtrude","SWEPT_FACE",FACE,{"disambiguationData":[OSD([subQ5,subQ4])]})]}),makeQuery(id+"F24.opExtrude","SWEPT_FACE",FACE,{"disambiguationData":[OSD([subQ3,subQ2])]})]}),makeQuery(id+"F25.opExtrude","SWEPT_FACE",FACE,{"disambiguationData":[OSD([subQ1,subQ0])]})]});}
            var sketch = newSketch(context, id + "F72", { "sketchPlane" : qUnion([Q0])});
            skLineSegment(sketch, "E126.bottom", {"start": v(-48.15, -24.54) * mm, "end": v(-36.96, -24.54) * mm});
            skLineSegment(sketch, "E126.top", {"start": v(-48.15, -20.94) * mm, "end": v(-36.96, -20.94) * mm});
            skLineSegment(sketch, "E126.left", {"start": v(-48.15, -24.54) * mm, "end": v(-48.15, -20.94) * mm});
            skLineSegment(sketch, "E126.right", {"start": v(-36.96, -24.54) * mm, "end": v(-36.96, -20.94) * mm});
            skSolve(sketch);
        }
        {
            var Q0;
            Q0 = qSketchRegion(id + "F72", true);
            extrude(context, id + "F73", {"entities" : qUnion([Q0]), "operationType" : NewBodyOperationType.ADD, "depth" : 10.92 * mm, "offsetDistance" : 25.4 * mm});
        }
        {
            var Q0;
            {var subQ0=sQuery(id+"F0.wireOp",EDGE,"E55");var subQ1=sQuery(id+"F0.wireOp",EDGE,"E42");var subQ2=sQuery(id+"F0.wireOp",EDGE,"E49");var subQ3=sQuery(id+"F0.wireOp",EDGE,"E26");var subQ4=sQuery(id+"F0.wireOp",EDGE,"E47");var subQ5=sQuery(id+"F0.wireOp",EDGE,"E5");var subQ6=sQuery(id+"F0.wireOp",EDGE,"E46");var subQ7=sQuery(id+"F0.wireOp",EDGE,"E36");var subQ8=sQuery(id+"F0.wireOp",EDGE,"E34");var subQ9=sQuery(id+"F0.wireOp",EDGE,"E53");var subQ10=sQuery(id+"F0.wireOp",EDGE,"E40");var subQ11=sQuery(id+"F0.wireOp",EDGE,"E38");var subQ12=makeQuery(id+"F3.opExtrude","CAP_FACE",FACE,{"disambiguationData":[OSD([sQuery(id+"F2.wireOp",EDGE,"E59.bottom"),sQuery(id+"F2.wireOp",EDGE,"E59.top"),sQuery(id+"F2.wireOp",EDGE,"E59.left"),sQuery(id+"F2.wireOp",EDGE,"E59.right")])],"isStart":true});var subQ13=sQuery(id+"F16.wireOp",EDGE,"E82");var subQ14=sQuery(id+"F12.wireOp",EDGE,"E79.bottom");var subQ16=sQuery(id+"F12.wireOp",EDGE,"E79.top");var subQ18=makeQuery(id+"F1.opExtrude","SWEPT_FACE",FACE,{"disambiguationData":[OSD([sQuery(id+"F0.wireOp",EDGE,"E10")])]});var subQ20=sQuery(id+"F12.wireOp",EDGE,"E79.right");var subQ21=sQuery(id+"F14.wireOp",EDGE,"E80.top");var subQ23=sQuery(id+"F14.wireOp",EDGE,"E80.bottom");var subQ25=makeQuery(id+"F1.opExtrude","SWEPT_FACE",FACE,{"disambiguationData":[OSD([sQuery(id+"F0.wireOp",EDGE,"E11")])]});var subQ26=makeQuery(id+"F15.boolean.opBoolean","MERGE",FACE,{"derivedFrom":[makeQuery(id+"F3.boolean.opBoolean","SPLIT",FACE,{"disambiguationData":[TD([subQ18])],"derivedFrom":subQ12}),makeQuery(id+"F13.boolean.opBoolean","COPY",FACE,{"derivedFrom":makeQuery(id+"F13.opExtrude","CAP_FACE",FACE,{"disambiguationData":[OSD([subQ14,subQ16,sQuery(id+"F12.wireOp",EDGE,"E79.left"),subQ20])],"isStart":false})}),makeQuery(id+"F15.opExtrude","CAP_FACE",FACE,{"disambiguationData":[OSD([subQ23,subQ21,sQuery(id+"F14.wireOp",EDGE,"E80.left"),sQuery(id+"F14.wireOp",EDGE,"E80.right")])],"isStart":false})]});Q0=makeQuery(id+"F25.boolean.opBoolean","MERGE",FACE,{"derivedFrom":[makeQuery(id+"F24.boolean.opBoolean","MERGE",FACE,{"derivedFrom":[makeQuery(id+"F3.boolean.opBoolean","SPLIT",FACE,{"disambiguationData":[TD([makeQuery(id+"F1.opExtrude","SWEPT_FACE",FACE,{"disambiguationData":[OSD([sQuery(id+"F0.wireOp",EDGE,"E7")])]})])],"derivedFrom":subQ12}),makeQuery(id+"F3.boolean.opBoolean","SPLIT",FACE,{"disambiguationData":[TD([makeQuery(id+"F1.opExtrude","SWEPT_FACE",FACE,{"disambiguationData":[OSD([sQuery(id+"F0.wireOp",EDGE,"E12")])]})])],"derivedFrom":subQ12}),makeQuery(id+"F23.boolean.opBoolean","MERGE",FACE,{"derivedFrom":[makeQuery(id+"F3.boolean.opBoolean","SPLIT",FACE,{"disambiguationData":[TD([makeQuery(id+"F1.opExtrude","SWEPT_FACE",FACE,{"disambiguationData":[OSD([sQuery(id+"F0.wireOp",EDGE,"E2")])]})])],"derivedFrom":subQ12}),makeQuery(id+"F22.boolean.opBoolean","MERGE",FACE,{"derivedFrom":[makeQuery(id+"F21.boolean.opBoolean","MERGE",FACE,{"derivedFrom":[makeQuery(id+"F19.boolean.opBoolean","MERGE",FACE,{"derivedFrom":[makeQuery(id+"F17.boolean.opBoolean","SPLIT",FACE,{"disambiguationData":[TD([subQ25])],"derivedFrom":subQ26}),makeQuery(id+"F17.boolean.opBoolean","SPLIT",FACE,{"disambiguationData":[TD([makeQuery(id+"F13.boolean.opBoolean","COPY",FACE,{"derivedFrom":makeQuery(id+"F13.opExtrude","SWEPT_FACE",FACE,{"disambiguationData":[OSD([subQ20])]})})])],"derivedFrom":subQ26}),makeQuery(id+"F19.opExtrude","SWEPT_FACE",FACE,{"disambiguationData":[OSD([subQ13])]})]}),makeQuery(id+"F20.boolean.opBoolean","MERGE",FACE,{"derivedFrom":[makeQuery(id+"F3.boolean.opBoolean","SPLIT",FACE,{"disambiguationData":[TD([makeQuery(id+"F1.opExtrude","SWEPT_FACE",FACE,{"disambiguationData":[OSD([sQuery(id+"F0.wireOp",EDGE,"E1")])]})])],"derivedFrom":subQ12}),makeQuery(id+"F3.boolean.opBoolean","SPLIT",FACE,{"disambiguationData":[TD([makeQuery(id+"F1.opExtrude","SWEPT_FACE",FACE,{"disambiguationData":[OSD([sQuery(id+"F0.wireOp",EDGE,"E33")])]})])],"derivedFrom":subQ12}),makeQuery(id+"F20.opExtrude","SWEPT_FACE",FACE,{"disambiguationData":[OSD([subQ11,subQ10,subQ9])]})]}),makeQuery(id+"F21.opExtrude","SWEPT_FACE",FACE,{"disambiguationData":[OSD([sQuery(id+"F0.wireOp",EDGE,"E21")])]})]}),makeQuery(id+"F22.opExtrude","SWEPT_FACE",FACE,{"disambiguationData":[OSD([subQ8,subQ7,subQ6])]})]}),makeQuery(id+"F23.opExtrude","SWEPT_FACE",FACE,{"disambiguationData":[OSD([subQ5,subQ4])]})]}),makeQuery(id+"F24.opExtrude","SWEPT_FACE",FACE,{"disambiguationData":[OSD([subQ3,subQ2])]})]}),makeQuery(id+"F25.opExtrude","SWEPT_FACE",FACE,{"disambiguationData":[OSD([subQ1,subQ0])]})]});}
            var sketch = newSketch(context, id + "F74", { "sketchPlane" : qUnion([Q0])});
            skLineSegment(sketch, "E127.bottom", {"start": v(-23.01, -16.77) * mm, "end": v(-25.27, -16.77) * mm});
            skLineSegment(sketch, "E127.top", {"start": v(-23.01, -10.07) * mm, "end": v(-25.27, -10.07) * mm});
            skLineSegment(sketch, "E127.left", {"start": v(-23.01, -16.77) * mm, "end": v(-23.01, -10.07) * mm});
            skLineSegment(sketch, "E127.right", {"start": v(-25.27, -16.77) * mm, "end": v(-25.27, -10.07) * mm});
            skSolve(sketch);
        }
        {
            var Q0;
            Q0 = qSketchRegion(id + "F74", true);
            extrude(context, id + "F75", {"entities" : qUnion([Q0]), "operationType" : NewBodyOperationType.ADD, "depth" : 16.26 * mm, "offsetDistance" : 25.4 * mm});
        }
        {
            var Q0;
            {var subQ0=sQuery(id+"F0.wireOp",EDGE,"E55");var subQ1=sQuery(id+"F0.wireOp",EDGE,"E42");var subQ2=sQuery(id+"F0.wireOp",EDGE,"E49");var subQ3=sQuery(id+"F0.wireOp",EDGE,"E26");var subQ4=sQuery(id+"F0.wireOp",EDGE,"E47");var subQ5=sQuery(id+"F0.wireOp",EDGE,"E5");var subQ6=sQuery(id+"F0.wireOp",EDGE,"E46");var subQ7=sQuery(id+"F0.wireOp",EDGE,"E36");var subQ8=sQuery(id+"F0.wireOp",EDGE,"E34");var subQ9=sQuery(id+"F0.wireOp",EDGE,"E53");var subQ10=sQuery(id+"F0.wireOp",EDGE,"E40");var subQ11=sQuery(id+"F0.wireOp",EDGE,"E38");var subQ12=makeQuery(id+"F3.opExtrude","CAP_FACE",FACE,{"disambiguationData":[OSD([sQuery(id+"F2.wireOp",EDGE,"E59.bottom"),sQuery(id+"F2.wireOp",EDGE,"E59.top"),sQuery(id+"F2.wireOp",EDGE,"E59.left"),sQuery(id+"F2.wireOp",EDGE,"E59.right")])],"isStart":true});var subQ13=sQuery(id+"F16.wireOp",EDGE,"E82");var subQ14=sQuery(id+"F12.wireOp",EDGE,"E79.bottom");var subQ16=sQuery(id+"F12.wireOp",EDGE,"E79.top");var subQ18=makeQuery(id+"F1.opExtrude","SWEPT_FACE",FACE,{"disambiguationData":[OSD([sQuery(id+"F0.wireOp",EDGE,"E10")])]});var subQ20=sQuery(id+"F12.wireOp",EDGE,"E79.right");var subQ21=sQuery(id+"F14.wireOp",EDGE,"E80.top");var subQ23=sQuery(id+"F14.wireOp",EDGE,"E80.bottom");var subQ25=makeQuery(id+"F1.opExtrude","SWEPT_FACE",FACE,{"disambiguationData":[OSD([sQuery(id+"F0.wireOp",EDGE,"E11")])]});var subQ26=makeQuery(id+"F15.boolean.opBoolean","MERGE",FACE,{"derivedFrom":[makeQuery(id+"F3.boolean.opBoolean","SPLIT",FACE,{"disambiguationData":[TD([subQ18])],"derivedFrom":subQ12}),makeQuery(id+"F13.boolean.opBoolean","COPY",FACE,{"derivedFrom":makeQuery(id+"F13.opExtrude","CAP_FACE",FACE,{"disambiguationData":[OSD([subQ14,subQ16,sQuery(id+"F12.wireOp",EDGE,"E79.left"),subQ20])],"isStart":false})}),makeQuery(id+"F15.opExtrude","CAP_FACE",FACE,{"disambiguationData":[OSD([subQ23,subQ21,sQuery(id+"F14.wireOp",EDGE,"E80.left"),sQuery(id+"F14.wireOp",EDGE,"E80.right")])],"isStart":false})]});Q0=makeQuery(id+"F25.boolean.opBoolean","MERGE",FACE,{"derivedFrom":[makeQuery(id+"F24.boolean.opBoolean","MERGE",FACE,{"derivedFrom":[makeQuery(id+"F3.boolean.opBoolean","SPLIT",FACE,{"disambiguationData":[TD([makeQuery(id+"F1.opExtrude","SWEPT_FACE",FACE,{"disambiguationData":[OSD([sQuery(id+"F0.wireOp",EDGE,"E7")])]})])],"derivedFrom":subQ12}),makeQuery(id+"F3.boolean.opBoolean","SPLIT",FACE,{"disambiguationData":[TD([makeQuery(id+"F1.opExtrude","SWEPT_FACE",FACE,{"disambiguationData":[OSD([sQuery(id+"F0.wireOp",EDGE,"E12")])]})])],"derivedFrom":subQ12}),makeQuery(id+"F23.boolean.opBoolean","MERGE",FACE,{"derivedFrom":[makeQuery(id+"F3.boolean.opBoolean","SPLIT",FACE,{"disambiguationData":[TD([makeQuery(id+"F1.opExtrude","SWEPT_FACE",FACE,{"disambiguationData":[OSD([sQuery(id+"F0.wireOp",EDGE,"E2")])]})])],"derivedFrom":subQ12}),makeQuery(id+"F22.boolean.opBoolean","MERGE",FACE,{"derivedFrom":[makeQuery(id+"F21.boolean.opBoolean","MERGE",FACE,{"derivedFrom":[makeQuery(id+"F19.boolean.opBoolean","MERGE",FACE,{"derivedFrom":[makeQuery(id+"F17.boolean.opBoolean","SPLIT",FACE,{"disambiguationData":[TD([subQ25])],"derivedFrom":subQ26}),makeQuery(id+"F17.boolean.opBoolean","SPLIT",FACE,{"disambiguationData":[TD([makeQuery(id+"F13.boolean.opBoolean","COPY",FACE,{"derivedFrom":makeQuery(id+"F13.opExtrude","SWEPT_FACE",FACE,{"disambiguationData":[OSD([subQ20])]})})])],"derivedFrom":subQ26}),makeQuery(id+"F19.opExtrude","SWEPT_FACE",FACE,{"disambiguationData":[OSD([subQ13])]})]}),makeQuery(id+"F20.boolean.opBoolean","MERGE",FACE,{"derivedFrom":[makeQuery(id+"F3.boolean.opBoolean","SPLIT",FACE,{"disambiguationData":[TD([makeQuery(id+"F1.opExtrude","SWEPT_FACE",FACE,{"disambiguationData":[OSD([sQuery(id+"F0.wireOp",EDGE,"E1")])]})])],"derivedFrom":subQ12}),makeQuery(id+"F3.boolean.opBoolean","SPLIT",FACE,{"disambiguationData":[TD([makeQuery(id+"F1.opExtrude","SWEPT_FACE",FACE,{"disambiguationData":[OSD([sQuery(id+"F0.wireOp",EDGE,"E33")])]})])],"derivedFrom":subQ12}),makeQuery(id+"F20.opExtrude","SWEPT_FACE",FACE,{"disambiguationData":[OSD([subQ11,subQ10,subQ9])]})]}),makeQuery(id+"F21.opExtrude","SWEPT_FACE",FACE,{"disambiguationData":[OSD([sQuery(id+"F0.wireOp",EDGE,"E21")])]})]}),makeQuery(id+"F22.opExtrude","SWEPT_FACE",FACE,{"disambiguationData":[OSD([subQ8,subQ7,subQ6])]})]}),makeQuery(id+"F23.opExtrude","SWEPT_FACE",FACE,{"disambiguationData":[OSD([subQ5,subQ4])]})]}),makeQuery(id+"F24.opExtrude","SWEPT_FACE",FACE,{"disambiguationData":[OSD([subQ3,subQ2])]})]}),makeQuery(id+"F25.opExtrude","SWEPT_FACE",FACE,{"disambiguationData":[OSD([subQ1,subQ0])]})]});}
            var sketch = newSketch(context, id + "F76", { "sketchPlane" : qUnion([Q0])});
            skLineSegment(sketch, "E128.bottom", {"start": v(-13.3, 33.65) * mm, "end": v(-6.73, 33.65) * mm});
            skLineSegment(sketch, "E128.top", {"start": v(-13.3, 20.23) * mm, "end": v(-6.73, 20.23) * mm});
            skLineSegment(sketch, "E128.left", {"start": v(-13.3, 33.65) * mm, "end": v(-13.3, 20.23) * mm});
            skLineSegment(sketch, "E128.right", {"start": v(-6.73, 33.65) * mm, "end": v(-6.73, 20.23) * mm});
            skLineSegment(sketch, "E129.bottom", {"start": v(10.98, 23.6) * mm, "end": v(6.25, 23.6) * mm});
            skLineSegment(sketch, "E129.top", {"start": v(10.98, 12.53) * mm, "end": v(6.25, 12.53) * mm});
            skLineSegment(sketch, "E129.left", {"start": v(10.98, 23.6) * mm, "end": v(10.98, 12.53) * mm});
            skLineSegment(sketch, "E129.right", {"start": v(6.25, 23.6) * mm, "end": v(6.25, 12.53) * mm});
            skSolve(sketch);
        }
        {
            var Q0;
            Q0 = qSketchRegion(id + "F76", true);
            extrude(context, id + "F77", {"entities" : qUnion([Q0]), "operationType" : NewBodyOperationType.ADD, "depth" : 10.67 * mm, "offsetDistance" : 25.4 * mm});
        }
    });
